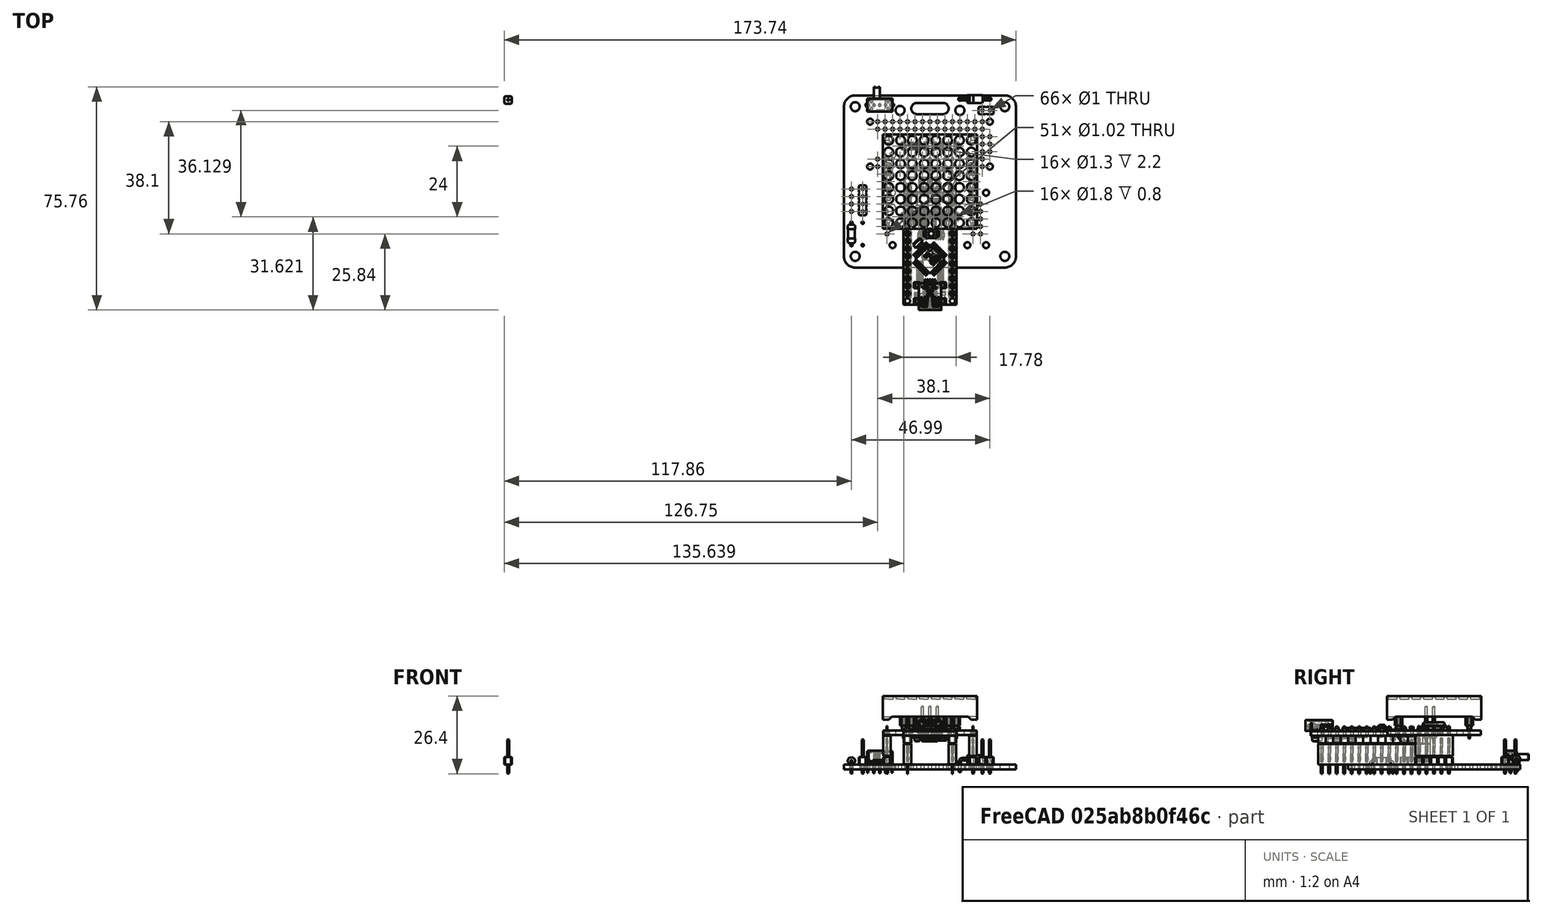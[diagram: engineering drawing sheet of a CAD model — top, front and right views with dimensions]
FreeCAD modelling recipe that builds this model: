
FCSTD DOCUMENT  (FreeCAD 0.20R29410 (Git))
Label: BagTag_v3
License: All rights reserved
LicenseURL: http://en.wikipedia.org/wiki/All_rights_reserved
objects: Part::Feature×202, App::Link×176, App::Part×9, Sketcher::SketchObject×3, PartDesign::CoordinateSystem×1
note: 206 computed .brp shape members not serialized (recipe doc carries the construction recipe); baked Part::Feature solids carry a one-line shape summary decoded from their .brp

FEATURE [PartDesign::CoordinateSystem] Local_CS_fc76
  AttacherType = Attacher::AttachEngine3D
  MapMode = 2
  Support = -> [X_Axis001]
FEATURE [Part::Feature] Pcb_fc76
  Placement = pos=(-88.9,83.82,0) rot=(0,0,1;0rad)
  shape: bbox 58.42 x 58.42 x 1.6 mm, 132 faces (baked)
FEATURE [Sketcher::SketchObject] PCB_Sketch_fc76
  FullyConstrained = false
  sketch-geometry (18):
    g0: LineSegment StartX=4.445 StartY=22.86 StartZ=0 EndX=-4.445 EndY=22.86 EndZ=0
    g1: LineSegment StartX=-25.4 StartY=29.21 StartZ=0 EndX=25.4 EndY=29.21 EndZ=0
    g2: LineSegment StartX=25.4 StartY=-29.21 StartZ=0 EndX=-25.4 EndY=-29.21 EndZ=0
    g3: LineSegment StartX=29.21 StartY=25.4 StartZ=0 EndX=29.21 EndY=-25.4 EndZ=0
    g4: LineSegment StartX=-4.445 StartY=26.67 StartZ=0 EndX=4.445 EndY=26.67 EndZ=0
    g5: LineSegment StartX=-29.21 StartY=-25.4 StartZ=0 EndX=-29.21 EndY=25.4 EndZ=0
    g6: ArcOfCircle CenterX=25.4 CenterY=25.4 CenterZ=0 NormalX=0 NormalY=0 NormalZ=-1 AngleXU=1.5708 Radius=3.81 StartAngle=0 EndAngle=1.5708
    g7: ArcOfCircle CenterX=-4.445 CenterY=24.765 CenterZ=0 NormalX=0 NormalY=0 NormalZ=-1 AngleXU=-1.5708 Radius=1.905 StartAngle=0 EndAngle=3.14159
    g8: ArcOfCircle CenterX=25.4 CenterY=-25.4 CenterZ=0 NormalX=0 NormalY=0 NormalZ=-1 AngleXU=3.14159 Radius=3.81 StartAngle=0 EndAngle=1.5708
    g9: ArcOfCircle CenterX=-25.4 CenterY=25.4 CenterZ=0 NormalX=0 NormalY=0 NormalZ=-1 AngleXU=-1.46676e-07 Radius=3.81 StartAngle=0 EndAngle=1.5708
    g10: ArcOfCircle CenterX=4.445 CenterY=24.765 CenterZ=0 NormalX=0 NormalY=0 NormalZ=-1 AngleXU=1.5708 Radius=1.905 StartAngle=0 EndAngle=3.14159
    g11: ArcOfCircle CenterX=-25.4 CenterY=-25.4 CenterZ=0 NormalX=0 NormalY=0 NormalZ=-1 AngleXU=-1.5708 Radius=3.81 StartAngle=0 EndAngle=1.5708
    g12: Circle CenterX=10.16 CenterY=24.13 CenterZ=0 NormalX=0 NormalY=0 NormalZ=1 AngleXU=0 Radius=1.54502
    g13: Circle CenterX=25.4 CenterY=25.4 CenterZ=0 NormalX=0 NormalY=0 NormalZ=1 AngleXU=0 Radius=1.524
    g14: Circle CenterX=-10.16 CenterY=24.13 CenterZ=0 NormalX=0 NormalY=0 NormalZ=1 AngleXU=0 Radius=1.524
    g15: Circle CenterX=-25.4 CenterY=-25.4 CenterZ=0 NormalX=0 NormalY=0 NormalZ=1 AngleXU=0 Radius=1.524
    g16: Circle CenterX=25.4 CenterY=-25.4 CenterZ=0 NormalX=0 NormalY=0 NormalZ=1 AngleXU=0 Radius=1.524
    g17: Circle CenterX=-25.4 CenterY=25.4 CenterZ=0 NormalX=0 NormalY=0 NormalZ=1 AngleXU=0 Radius=1.524
  constraints (12):
    c: Coincident(g5,g11)
    c: Coincident(g5,g9)
    c: Coincident(g2,g11)
    c: Coincident(g1,g9)
    c: Coincident(g0,g7)
    c: Coincident(g4,g7)
    c: Coincident(g0,g10)
    c: Coincident(g4,g10)
    c: Coincident(g2,g8)
    c: Coincident(g1,g6)
    c: Coincident(g3,g8)
    c: Coincident(g3,g6)
FEATURE [App::Part] Board_Geoms_fc76
  Group = -> [Pcb_fc76,PCB_Sketch_fc76]
  Origin = -> Origin
FEATURE [Part::Feature] Shape  label="J203_PinHeader_1x01_P254mm_Vertical_da6c4aed0287"
  Placement = pos=(-143.256,27.686,0) rot=(0,0,1;1.5708rad)
  shape: bbox 2.54 x 2.54 x 11.54 mm, 28 faces (baked)
FEATURE [App::Link] J203_PinHeader_1x01_P254mm_Vertical_da6c4aed0287_ln_  label="J129_PinHeader_1x01_P254mm_Vertical_773ae547e81d"
  LinkPlacement = pos=(-96.012,34.036,0) rot=(0,0,1;1.5708rad)
  LinkedObject = -> Shape
  Placement = pos=(-96.012,34.036,0) rot=(0,0,1;1.5708rad)
FEATURE [App::Link] J203_PinHeader_1x01_P254mm_Vertical_da6c4aed0287_ln_001  label="J118_PinHeader_1x01_P254mm_Vertical_5aa259a9185c"
  LinkPlacement = pos=(-98.552,39.116,0) rot=(0,0,1;1.5708rad)
  LinkedObject = -> Shape
  Placement = pos=(-98.552,39.116,0) rot=(0,0,1;1.5708rad)
FEATURE [App::Link] J203_PinHeader_1x01_P254mm_Vertical_da6c4aed0287_ln_002  label="J208_PinHeader_1x01_P254mm_Vertical_72f53bb47756"
  LinkPlacement = pos=(-143.256,25.146,0) rot=(0,0,1;1.5708rad)
  LinkedObject = -> Shape
  Placement = pos=(-143.256,25.146,0) rot=(0,0,1;1.5708rad)
FEATURE [App::Link] J203_PinHeader_1x01_P254mm_Vertical_da6c4aed0287_ln_003  label="J192_PinHeader_1x01_P254mm_Vertical_2792789bb18d"
  LinkPlacement = pos=(-130.556,22.098,0) rot=(0,0,1;1.5708rad)
  LinkedObject = -> Shape
  Placement = pos=(-130.556,22.098,0) rot=(0,0,1;1.5708rad)
FEATURE [App::Link] J203_PinHeader_1x01_P254mm_Vertical_da6c4aed0287_ln_004  label="J112_PinHeader_1x01_P254mm_Vertical_6a244c9ca252"
  LinkPlacement = pos=(-101.092,41.656,0) rot=(0,0,1;1.5708rad)
  LinkedObject = -> Shape
  Placement = pos=(-101.092,41.656,0) rot=(0,0,1;1.5708rad)
FEATURE [App::Link] J203_PinHeader_1x01_P254mm_Vertical_da6c4aed0287_ln_005  label="J137_PinHeader_1x01_P254mm_Vertical_9c543508d3f7"
  LinkPlacement = pos=(-101.092,28.956,0) rot=(0,0,1;1.5708rad)
  LinkedObject = -> Shape
  Placement = pos=(-101.092,28.956,0) rot=(0,0,1;1.5708rad)
FEATURE [App::Link] J203_PinHeader_1x01_P254mm_Vertical_da6c4aed0287_ln_006  label="J141_PinHeader_1x01_P254mm_Vertical_27754063a736"
  LinkPlacement = pos=(-103.632,26.416,0) rot=(0,0,1;1.5708rad)
  LinkedObject = -> Shape
  Placement = pos=(-103.632,26.416,0) rot=(0,0,1;1.5708rad)
FEATURE [App::Link] J203_PinHeader_1x01_P254mm_Vertical_da6c4aed0287_ln_007  label="J127_PinHeader_1x01_P254mm_Vertical_64cb25116942"
  LinkPlacement = pos=(-101.092,34.036,0) rot=(0,0,1;1.5708rad)
  LinkedObject = -> Shape
  Placement = pos=(-101.092,34.036,0) rot=(0,0,1;1.5708rad)
FEATURE [App::Link] J203_PinHeader_1x01_P254mm_Vertical_da6c4aed0287_ln_008  label="J109_PinHeader_1x01_P254mm_Vertical_46e97698a8e3"
  LinkPlacement = pos=(-96.012,44.196,0) rot=(0,0,1;1.5708rad)
  LinkedObject = -> Shape
  Placement = pos=(-96.012,44.196,0) rot=(0,0,1;1.5708rad)
FEATURE [App::Link] J203_PinHeader_1x01_P254mm_Vertical_da6c4aed0287_ln_009  label="J136_PinHeader_1x01_P254mm_Vertical_3277878d9fcc"
  LinkPlacement = pos=(-103.632,28.956,0) rot=(0,0,1;1.5708rad)
  LinkedObject = -> Shape
  Placement = pos=(-103.632,28.956,0) rot=(0,0,1;1.5708rad)
FEATURE [App::Link] J203_PinHeader_1x01_P254mm_Vertical_da6c4aed0287_ln_010  label="J174_PinHeader_1x01_P254mm_Vertical_6a619a310b17"
  LinkPlacement = pos=(-111.252,22.352,0) rot=(0,0,1;1.5708rad)
  LinkedObject = -> Shape
  Placement = pos=(-111.252,22.352,0) rot=(0,0,1;1.5708rad)
FEATURE [App::Link] J203_PinHeader_1x01_P254mm_Vertical_da6c4aed0287_ln_011  label="J163_PinHeader_1x01_P254mm_Vertical_eca1b71ce0e1"
  LinkPlacement = pos=(-113.792,27.432,0) rot=(0,0,1;1.5708rad)
  LinkedObject = -> Shape
  Placement = pos=(-113.792,27.432,0) rot=(0,0,1;1.5708rad)
FEATURE [App::Link] J203_PinHeader_1x01_P254mm_Vertical_da6c4aed0287_ln_012  label="J221_PinHeader_1x01_P254mm_Vertical_e87cc0828aff"
  LinkPlacement = pos=(-91.694,43.688,0) rot=(0,0,1;1.5708rad)
  LinkedObject = -> Shape
  Placement = pos=(-91.694,43.688,0) rot=(0,0,1;1.5708rad)
FEATURE [App::Link] J203_PinHeader_1x01_P254mm_Vertical_da6c4aed0287_ln_013  label="J145_PinHeader_1x01_P254mm_Vertical_00ab3d87ffcd"
  LinkPlacement = pos=(-106.172,23.876,0) rot=(0,0,1;1.5708rad)
  LinkedObject = -> Shape
  Placement = pos=(-106.172,23.876,0) rot=(0,0,1;1.5708rad)
FEATURE [App::Link] J203_PinHeader_1x01_P254mm_Vertical_da6c4aed0287_ln_014  label="J177_PinHeader_1x01_P254mm_Vertical_e80f5348a3fd"
  LinkPlacement = pos=(-116.332,19.812,0) rot=(0,0,1;1.5708rad)
  LinkedObject = -> Shape
  Placement = pos=(-116.332,19.812,0) rot=(0,0,1;1.5708rad)
FEATURE [App::Link] J203_PinHeader_1x01_P254mm_Vertical_da6c4aed0287_ln_015  label="J207_PinHeader_1x01_P254mm_Vertical_62e98df2bb86"
  LinkPlacement = pos=(-145.796,25.146,0) rot=(0,0,1;1.5708rad)
  LinkedObject = -> Shape
  Placement = pos=(-145.796,25.146,0) rot=(0,0,1;1.5708rad)
FEATURE [App::Link] J203_PinHeader_1x01_P254mm_Vertical_da6c4aed0287_ln_016  label="J191_PinHeader_1x01_P254mm_Vertical_de5b5ec60197"
  LinkPlacement = pos=(-133.096,22.098,0) rot=(0,0,1;1.5708rad)
  LinkedObject = -> Shape
  Placement = pos=(-133.096,22.098,0) rot=(0,0,1;1.5708rad)
FEATURE [App::Link] J203_PinHeader_1x01_P254mm_Vertical_da6c4aed0287_ln_017  label="J166_PinHeader_1x01_P254mm_Vertical_84919f920f7b"
  LinkPlacement = pos=(-118.872,24.892,0) rot=(0,0,1;1.5708rad)
  LinkedObject = -> Shape
  Placement = pos=(-118.872,24.892,0) rot=(0,0,1;1.5708rad)
FEATURE [App::Link] J203_PinHeader_1x01_P254mm_Vertical_da6c4aed0287_ln_018  label="J153_PinHeader_1x01_P254mm_Vertical_de25c8d6ebfc"
  LinkPlacement = pos=(-98.552,21.336,0) rot=(0,0,1;1.5708rad)
  LinkedObject = -> Shape
  Placement = pos=(-98.552,21.336,0) rot=(0,0,1;1.5708rad)
FEATURE [App::Link] J203_PinHeader_1x01_P254mm_Vertical_da6c4aed0287_ln_019  label="J146_PinHeader_1x01_P254mm_Vertical_6cd363f12a80"
  LinkPlacement = pos=(-103.632,23.876,0) rot=(0,0,1;1.5708rad)
  LinkedObject = -> Shape
  Placement = pos=(-103.632,23.876,0) rot=(0,0,1;1.5708rad)
FEATURE [App::Link] J203_PinHeader_1x01_P254mm_Vertical_da6c4aed0287_ln_020  label="J160_PinHeader_1x01_P254mm_Vertical_7b98299fb2b6"
  LinkPlacement = pos=(-121.412,27.432,0) rot=(0,0,1;1.5708rad)
  LinkedObject = -> Shape
  Placement = pos=(-121.412,27.432,0) rot=(0,0,1;1.5708rad)
FEATURE [App::Link] J203_PinHeader_1x01_P254mm_Vertical_da6c4aed0287_ln_021  label="J214_PinHeader_1x01_P254mm_Vertical_d33f2c13bd96"
  LinkPlacement = pos=(-140.716,22.606,0) rot=(0,0,1;1.5708rad)
  LinkedObject = -> Shape
  Placement = pos=(-140.716,22.606,0) rot=(0,0,1;1.5708rad)
FEATURE [App::Link] J203_PinHeader_1x01_P254mm_Vertical_da6c4aed0287_ln_022  label="J142_PinHeader_1x01_P254mm_Vertical_ebb3536fd29e"
  LinkPlacement = pos=(-101.092,26.416,0) rot=(0,0,1;1.5708rad)
  LinkedObject = -> Shape
  Placement = pos=(-101.092,26.416,0) rot=(0,0,1;1.5708rad)
FEATURE [App::Link] J203_PinHeader_1x01_P254mm_Vertical_da6c4aed0287_ln_023  label="J126_PinHeader_1x01_P254mm_Vertical_9a14729430aa"
  LinkPlacement = pos=(-103.632,34.036,0) rot=(0,0,1;1.5708rad)
  LinkedObject = -> Shape
  Placement = pos=(-103.632,34.036,0) rot=(0,0,1;1.5708rad)
FEATURE [App::Link] J203_PinHeader_1x01_P254mm_Vertical_da6c4aed0287_ln_024  label="J198_PinHeader_1x01_P254mm_Vertical_e60d4ac48af7"
  LinkPlacement = pos=(-128.016,19.558,0) rot=(0,0,1;1.5708rad)
  LinkedObject = -> Shape
  Placement = pos=(-128.016,19.558,0) rot=(0,0,1;1.5708rad)
FEATURE [App::Link] J203_PinHeader_1x01_P254mm_Vertical_da6c4aed0287_ln_025  label="J167_PinHeader_1x01_P254mm_Vertical_5f2264147a32"
  LinkPlacement = pos=(-116.332,24.892,0) rot=(0,0,1;1.5708rad)
  LinkedObject = -> Shape
  Placement = pos=(-116.332,24.892,0) rot=(0,0,1;1.5708rad)
FEATURE [App::Link] J203_PinHeader_1x01_P254mm_Vertical_da6c4aed0287_ln_026  label="J175_PinHeader_1x01_P254mm_Vertical_2f2c6f5fa7e0"
  LinkPlacement = pos=(-121.412,19.812,0) rot=(0,0,1;1.5708rad)
  LinkedObject = -> Shape
  Placement = pos=(-121.412,19.812,0) rot=(0,0,1;1.5708rad)
FEATURE [App::Link] J203_PinHeader_1x01_P254mm_Vertical_da6c4aed0287_ln_027  label="J185_PinHeader_1x01_P254mm_Vertical_64dd41409d9f"
  LinkPlacement = pos=(-135.636,24.638,0) rot=(0,0,1;1.5708rad)
  LinkedObject = -> Shape
  Placement = pos=(-135.636,24.638,0) rot=(0,0,1;1.5708rad)
FEATURE [App::Link] J203_PinHeader_1x01_P254mm_Vertical_da6c4aed0287_ln_028  label="J128_PinHeader_1x01_P254mm_Vertical_14a406c96dca"
  LinkPlacement = pos=(-98.552,34.036,0) rot=(0,0,1;1.5708rad)
  LinkedObject = -> Shape
  Placement = pos=(-98.552,34.036,0) rot=(0,0,1;1.5708rad)
FEATURE [App::Link] J203_PinHeader_1x01_P254mm_Vertical_da6c4aed0287_ln_029  label="J212_PinHeader_1x01_P254mm_Vertical_684e6d7036d3"
  LinkPlacement = pos=(-145.796,22.606,0) rot=(0,0,1;1.5708rad)
  LinkedObject = -> Shape
  Placement = pos=(-145.796,22.606,0) rot=(0,0,1;1.5708rad)
FEATURE [App::Link] J203_PinHeader_1x01_P254mm_Vertical_da6c4aed0287_ln_030  label="J181_PinHeader_1x01_P254mm_Vertical_3395830e7b0b"
  LinkPlacement = pos=(-133.096,27.178,0) rot=(0,0,1;1.5708rad)
  LinkedObject = -> Shape
  Placement = pos=(-133.096,27.178,0) rot=(0,0,1;1.5708rad)
FEATURE [App::Link] J203_PinHeader_1x01_P254mm_Vertical_da6c4aed0287_ln_031  label="J158_PinHeader_1x01_P254mm_Vertical_ad3d40650960"
  LinkPlacement = pos=(-98.552,18.796,0) rot=(0,0,1;1.5708rad)
  LinkedObject = -> Shape
  Placement = pos=(-98.552,18.796,0) rot=(0,0,1;1.5708rad)
FEATURE [App::Link] J203_PinHeader_1x01_P254mm_Vertical_da6c4aed0287_ln_032  label="J104_PinHeader_1x01_P254mm_Vertical_8b62ba1c48d5"
  LinkPlacement = pos=(-96.012,46.736,0) rot=(0,0,1;1.5708rad)
  LinkedObject = -> Shape
  Placement = pos=(-96.012,46.736,0) rot=(0,0,1;1.5708rad)
FEATURE [App::Link] J203_PinHeader_1x01_P254mm_Vertical_da6c4aed0287_ln_033  label="J197_PinHeader_1x01_P254mm_Vertical_d9d08025a7fb"
  LinkPlacement = pos=(-130.556,19.558,0) rot=(0,0,1;1.5708rad)
  LinkedObject = -> Shape
  Placement = pos=(-130.556,19.558,0) rot=(0,0,1;1.5708rad)
FEATURE [App::Link] J203_PinHeader_1x01_P254mm_Vertical_da6c4aed0287_ln_034  label="J195_PinHeader_1x01_P254mm_Vertical_3bb2cf8e585d"
  LinkPlacement = pos=(-135.636,19.558,0) rot=(0,0,1;1.5708rad)
  LinkedObject = -> Shape
  Placement = pos=(-135.636,19.558,0) rot=(0,0,1;1.5708rad)
FEATURE [App::Link] J203_PinHeader_1x01_P254mm_Vertical_da6c4aed0287_ln_035  label="J204_PinHeader_1x01_P254mm_Vertical_428c39a7f71f"
  LinkPlacement = pos=(-140.716,27.686,0) rot=(0,0,1;1.5708rad)
  LinkedObject = -> Shape
  Placement = pos=(-140.716,27.686,0) rot=(0,0,1;1.5708rad)
FEATURE [App::Link] J203_PinHeader_1x01_P254mm_Vertical_da6c4aed0287_ln_036  label="J242_PinHeader_1x01_P254mm_Vertical_00fbceee7ab9"
  LinkPlacement = pos=(-86.614,20.828,0) rot=(0,0,1;1.5708rad)
  LinkedObject = -> Shape
  Placement = pos=(-86.614,20.828,0) rot=(0,0,1;1.5708rad)
FEATURE [App::Link] J203_PinHeader_1x01_P254mm_Vertical_da6c4aed0287_ln_037  label="J235_PinHeader_1x01_P254mm_Vertical_68c39cdf1477"
  LinkPlacement = pos=(-86.614,38.608,0) rot=(0,0,1;1.5708rad)
  LinkedObject = -> Shape
  Placement = pos=(-86.614,38.608,0) rot=(0,0,1;1.5708rad)
FEATURE [App::Link] J203_PinHeader_1x01_P254mm_Vertical_da6c4aed0287_ln_038  label="J215_PinHeader_1x01_P254mm_Vertical_30fb8c6109c9"
  LinkPlacement = pos=(-150.876,20.066,0) rot=(0,0,1;1.5708rad)
  LinkedObject = -> Shape
  Placement = pos=(-150.876,20.066,0) rot=(0,0,1;1.5708rad)
FEATURE [App::Link] J203_PinHeader_1x01_P254mm_Vertical_da6c4aed0287_ln_039  label="J155_PinHeader_1x01_P254mm_Vertical_cbb93bdeda80"
  LinkPlacement = pos=(-106.172,18.796,0) rot=(0,0,1;1.5708rad)
  LinkedObject = -> Shape
  Placement = pos=(-106.172,18.796,0) rot=(0,0,1;1.5708rad)
FEATURE [App::Link] J203_PinHeader_1x01_P254mm_Vertical_da6c4aed0287_ln_040  label="J134_PinHeader_1x01_P254mm_Vertical_c71becf67217"
  LinkPlacement = pos=(-96.012,31.496,0) rot=(0,0,1;1.5708rad)
  LinkedObject = -> Shape
  Placement = pos=(-96.012,31.496,0) rot=(0,0,1;1.5708rad)
FEATURE [App::Link] J203_PinHeader_1x01_P254mm_Vertical_da6c4aed0287_ln_041  label="J216_PinHeader_1x01_P254mm_Vertical_3caf071db488"
  LinkPlacement = pos=(-148.336,20.066,0) rot=(0,0,1;1.5708rad)
  LinkedObject = -> Shape
  Placement = pos=(-148.336,20.066,0) rot=(0,0,1;1.5708rad)
FEATURE [App::Link] J203_PinHeader_1x01_P254mm_Vertical_da6c4aed0287_ln_042  label="J184_PinHeader_1x01_P254mm_Vertical_249d3775cc33"
  LinkPlacement = pos=(-125.476,27.178,0) rot=(0,0,1;1.5708rad)
  LinkedObject = -> Shape
  Placement = pos=(-125.476,27.178,0) rot=(0,0,1;1.5708rad)
FEATURE [App::Link] J203_PinHeader_1x01_P254mm_Vertical_da6c4aed0287_ln_043  label="J190_PinHeader_1x01_P254mm_Vertical_a719b4abe7b1"
  LinkPlacement = pos=(-135.636,22.098,0) rot=(0,0,1;1.5708rad)
  LinkedObject = -> Shape
  Placement = pos=(-135.636,22.098,0) rot=(0,0,1;1.5708rad)
FEATURE [Part::Feature] Part__Feature  label="FC_16_cp_sp"
  shape: bbox 31.75 x 31.75 x 1.6 mm, 36 faces (baked)
FEATURE [Part::Feature] Part__Feature001  label="FC_16_cp_sp001"
  shape: bbox 1.25 x 2 x 1.25 mm, 28 faces (baked)
FEATURE [Part::Feature] Part__Feature002  label="FC_16_cp_sp002"
  shape: bbox 32 x 32 x 13.3 mm, 258 faces (baked)
FEATURE [Part::Feature] Part__Feature003  label="FC_16_cp_sp003"
  shape: bbox 20.32 x 2.54 x 3 mm, 94 faces (baked)
FEATURE [Part::Feature] Part__Feature004  label="FC_16_cp_sp004"
  shape: bbox 1.8 x 1.8 x 7.4 mm, 10 faces (baked)
FEATURE [Part::Feature] Part__Feature005  label="FC_16_cp_sp005"
  shape: bbox 1.8 x 1.8 x 7.4 mm, 10 faces (baked)
FEATURE [Part::Feature] Part__Feature006  label="FC_16_cp_sp006"
  shape: bbox 1.8 x 1.8 x 7.4 mm, 10 faces (baked)
FEATURE [Part::Feature] Part__Feature007  label="FC_16_cp_sp007"
  shape: bbox 1.8 x 1.8 x 7.4 mm, 10 faces (baked)
FEATURE [Part::Feature] Part__Feature008  label="FC_16_cp_sp008"
  shape: bbox 1.8 x 1.8 x 7.4 mm, 10 faces (baked)
FEATURE [Part::Feature] Part__Feature009  label="FC_16_cp_sp009"
  shape: bbox 1.8 x 1.8 x 7.4 mm, 10 faces (baked)
FEATURE [Part::Feature] Part__Feature010  label="FC_16_cp_sp010"
  shape: bbox 1.8 x 1.8 x 7.4 mm, 10 faces (baked)
FEATURE [Part::Feature] Part__Feature011  label="FC_16_cp_sp011"
  shape: bbox 1.8 x 1.8 x 7.4 mm, 10 faces (baked)
FEATURE [Part::Feature] Part__Feature012  label="FC_16_cp_sp012"
  shape: bbox 1 x 1 x 2.04 mm, 27 faces (baked)
FEATURE [Part::Feature] Part__Feature013  label="FC_16_cp_sp013"
  shape: bbox 1 x 1 x 2.04 mm, 27 faces (baked)
FEATURE [Part::Feature] Part__Feature014  label="FC_16_cp_sp014"
  shape: bbox 1 x 1 x 2.04 mm, 27 faces (baked)
FEATURE [Part::Feature] Part__Feature015  label="FC_16_cp_sp015"
  shape: bbox 1 x 1 x 2.04 mm, 27 faces (baked)
FEATURE [Part::Feature] Part__Feature016  label="FC_16_cp_sp016"
  shape: bbox 1 x 1 x 2.04 mm, 27 faces (baked)
FEATURE [Part::Feature] Part__Feature017  label="FC_16_cp_sp017"
  shape: bbox 1 x 1 x 2.04 mm, 27 faces (baked)
FEATURE [Part::Feature] Part__Feature018  label="FC_16_cp_sp018"
  shape: bbox 1 x 1 x 2.04 mm, 27 faces (baked)
FEATURE [Part::Feature] Part__Feature019  label="FC_16_cp_sp019"
  shape: bbox 1 x 1 x 2.04 mm, 27 faces (baked)
FEATURE [Part::Feature] Part__Feature020  label="FC_16_cp_sp020"
  shape: bbox 20.32 x 2.54 x 3 mm, 94 faces (baked)
FEATURE [Part::Feature] Part__Feature021  label="FC_16_cp_sp021"
  shape: bbox 1.8 x 1.8 x 7.4 mm, 10 faces (baked)
FEATURE [Part::Feature] Part__Feature022  label="FC_16_cp_sp022"
  shape: bbox 1.8 x 1.8 x 7.4 mm, 10 faces (baked)
FEATURE [Part::Feature] Part__Feature023  label="FC_16_cp_sp023"
  shape: bbox 1.8 x 1.8 x 7.4 mm, 10 faces (baked)
FEATURE [Part::Feature] Part__Feature024  label="FC_16_cp_sp024"
  shape: bbox 1.8 x 1.8 x 7.4 mm, 10 faces (baked)
FEATURE [Part::Feature] Part__Feature025  label="FC_16_cp_sp025"
  shape: bbox 1.8 x 1.8 x 7.4 mm, 10 faces (baked)
FEATURE [Part::Feature] Part__Feature026  label="FC_16_cp_sp026"
  shape: bbox 1.8 x 1.8 x 7.4 mm, 10 faces (baked)
FEATURE [Part::Feature] Part__Feature027  label="FC_16_cp_sp027"
  shape: bbox 1.8 x 1.8 x 7.4 mm, 10 faces (baked)
FEATURE [Part::Feature] Part__Feature028  label="FC_16_cp_sp028"
  shape: bbox 1.8 x 1.8 x 7.4 mm, 10 faces (baked)
FEATURE [Part::Feature] Part__Feature029  label="FC_16_cp_sp029"
  shape: bbox 1 x 1 x 2.04 mm, 27 faces (baked)
FEATURE [Part::Feature] Part__Feature030  label="FC_16_cp_sp030"
  shape: bbox 1 x 1 x 2.04 mm, 27 faces (baked)
FEATURE [Part::Feature] Part__Feature031  label="FC_16_cp_sp031"
  shape: bbox 1 x 1 x 2.04 mm, 27 faces (baked)
FEATURE [Part::Feature] Part__Feature032  label="FC_16_cp_sp032"
  shape: bbox 1 x 1 x 2.04 mm, 27 faces (baked)
FEATURE [Part::Feature] Part__Feature033  label="FC_16_cp_sp033"
  shape: bbox 1 x 1 x 2.04 mm, 27 faces (baked)
FEATURE [Part::Feature] Part__Feature034  label="FC_16_cp_sp034"
  shape: bbox 1 x 1 x 2.04 mm, 27 faces (baked)
FEATURE [Part::Feature] Part__Feature035  label="FC_16_cp_sp035"
  shape: bbox 1 x 1 x 2.04 mm, 27 faces (baked)
FEATURE [Part::Feature] Part__Feature036  label="FC_16_cp_sp036"
  shape: bbox 1 x 1 x 2.04 mm, 27 faces (baked)
FEATURE [Part::Feature] Part__Feature037  label="FC_16_cp_sp037"
  shape: bbox 2 x 1.2 x 0.45 mm, 26 faces (baked)
FEATURE [Part::Feature] Part__Feature038  label="FC_16_cp_sp038"
  shape: bbox 15.4 x 10.3 x 2.75 mm, 396 faces (baked)
FEATURE [Part::Feature] Part__Feature039  label="FC_16_cp_sp039"
  shape: bbox 2 x 1.25 x 1.25 mm, 28 faces (baked)
FEATURE [Part::Feature] Part__Feature040  label="FC_16_cp_sp040"
  shape: bbox 2.54 x 12.7 x 10.1 mm, 165 faces (baked)
FEATURE [Part::Feature] Part__Feature041  label="FC_16_cp_sp041"
  shape: bbox 2.54 x 12.7 x 10.1 mm, 165 faces (baked)
FEATURE [Part::Feature] Part__Feature042  label="FC_16_cp_sp042"
  shape: bbox 2.54 x 12.7 x 11.54 mm, 124 faces (baked)
FEATURE [Part::Feature] Part__Feature043  label="FC_16_cp_sp043"
  shape: bbox 2.54 x 12.7 x 11.54 mm, 124 faces (baked)
FEATURE [Part::Feature] Part__Feature044  label="FC_16_cp_sp044"
  shape: bbox 31.6 x 31.6 x 2e-07 mm, 1 faces, 0 solids (baked)
FEATURE [Part::Feature] Part__Feature045  label="FC_16_cp_sp045"
  shape: bbox 0.385 x 9.655 x 2e-07 mm, 1 faces, 0 solids (baked)
FEATURE [Part::Feature] Part__Feature046  label="FC_16_cp_sp046"
  shape: bbox 0.385 x 7.84 x 2e-07 mm, 1 faces, 0 solids (baked)
FEATURE [Part::Feature] Part__Feature047  label="FC_16_cp_sp047"
  shape: bbox 5.284 x 2.531 x 2e-07 mm, 1 faces, 0 solids (baked)
FEATURE [Part::Feature] Part__Feature048  label="FC_16_cp_sp048"
  shape: bbox 3.957 x 2.466 x 2e-07 mm, 1 faces, 0 solids (baked)
FEATURE [Part::Feature] Part__Feature049  label="FC_16_cp_sp049"
  shape: bbox 3.273 x 1.422 x 2e-07 mm, 1 faces, 0 solids (baked)
FEATURE [Part::Feature] Part__Feature050  label="FC_16_cp_sp050"
  shape: bbox 3.273 x 1.422 x 2e-07 mm, 1 faces, 0 solids (baked)
FEATURE [Part::Feature] Part__Feature051  label="FC_16_cp_sp051"
  shape: bbox 3.273 x 1.422 x 2e-07 mm, 1 faces, 0 solids (baked)
FEATURE [Part::Feature] Part__Feature052  label="FC_16_cp_sp052"
  shape: bbox 3.273 x 1.422 x 2e-07 mm, 1 faces, 0 solids (baked)
FEATURE [Part::Feature] Part__Feature053  label="FC_16_cp_sp053"
  shape: bbox 3.273 x 1.422 x 2e-07 mm, 1 faces, 0 solids (baked)
FEATURE [Part::Feature] Part__Feature054  label="FC_16_cp_sp054"
  shape: bbox 3.273 x 1.422 x 2e-07 mm, 1 faces, 0 solids (baked)
FEATURE [Part::Feature] Part__Feature055  label="FC_16_cp_sp055"
  shape: bbox 3.273 x 1.422 x 2e-07 mm, 1 faces, 0 solids (baked)
FEATURE [Part::Feature] Part__Feature056  label="FC_16_cp_sp056"
  shape: bbox 3.273 x 1.422 x 2e-07 mm, 1 faces, 0 solids (baked)
FEATURE [Part::Feature] Part__Feature057  label="FC_16_cp_sp057"
  shape: bbox 3.273 x 1.422 x 2e-07 mm, 1 faces, 0 solids (baked)
FEATURE [Part::Feature] Part__Feature058  label="FC_16_cp_sp058"
  shape: bbox 3.267 x 1.403 x 2e-07 mm, 1 faces, 0 solids (baked)
FEATURE [Part::Feature] Part__Feature059  label="FC_16_cp_sp059"
  shape: bbox 1.15 x 0.7688 x 2e-07 mm, 1 faces, 0 solids (baked)
FEATURE [Part::Feature] Part__Feature060  label="FC_16_cp_sp060"
  shape: bbox 1.15 x 0.7687 x 2e-07 mm, 1 faces, 0 solids (baked)
FEATURE [Part::Feature] Part__Feature061  label="FC_16_cp_sp061"
  shape: bbox 1.15 x 0.7687 x 2e-07 mm, 1 faces, 0 solids (baked)
FEATURE [Part::Feature] Part__Feature062  label="FC_16_cp_sp062"
  shape: bbox 1.15 x 0.7687 x 2e-07 mm, 1 faces, 0 solids (baked)
FEATURE [Part::Feature] Part__Feature063  label="FC_16_cp_sp063"
  shape: bbox 1.149 x 0.7214 x 2e-07 mm, 1 faces, 0 solids (baked)
FEATURE [Part::Feature] Part__Feature064  label="FC_16_cp_sp064"
  shape: bbox 1.149 x 0.7214 x 2e-07 mm, 1 faces, 0 solids (baked)
FEATURE [Part::Feature] Part__Feature065  label="FC_16_cp_sp065"
  shape: bbox 1.15 x 0.7192 x 2e-07 mm, 1 faces, 0 solids (baked)
FEATURE [Part::Feature] Part__Feature066  label="FC_16_cp_sp066"
  shape: bbox 1.15 x 0.7192 x 2e-07 mm, 1 faces, 0 solids (baked)
FEATURE [Part::Feature] Part__Feature067  label="FC_16_cp_sp067"
  shape: bbox 1.15 x 0.7192 x 2e-07 mm, 1 faces, 0 solids (baked)
FEATURE [Part::Feature] Part__Feature068  label="FC_16_cp_sp068"
  shape: bbox 1.15 x 0.7191 x 2e-07 mm, 1 faces, 0 solids (baked)
FEATURE [Part::Feature] Part__Feature069  label="FC_16_cp_sp069"
  shape: bbox 1.145 x 0.719 x 2e-07 mm, 1 faces, 0 solids (baked)
FEATURE [Part::Feature] Part__Feature070  label="FC_16_cp_sp070"
  shape: bbox 1.145 x 0.719 x 2e-07 mm, 1 faces, 0 solids (baked)
FEATURE [Part::Feature] Part__Feature071  label="FC_16_cp_sp071"
  shape: bbox 1.096 x 0.7666 x 2e-07 mm, 1 faces, 0 solids (baked)
FEATURE [Part::Feature] Part__Feature072  label="FC_16_cp_sp072"
  shape: bbox 1.1 x 0.719 x 2e-07 mm, 1 faces, 0 solids (baked)
FEATURE [Part::Feature] Part__Feature073  label="FC_16_cp_sp073"
  shape: bbox 1.1 x 0.719 x 2e-07 mm, 1 faces, 0 solids (baked)
FEATURE [Part::Feature] Part__Feature074  label="FC_16_cp_sp074"
  shape: bbox 1.1 x 0.719 x 2e-07 mm, 1 faces, 0 solids (baked)
FEATURE [Part::Feature] Part__Feature075  label="FC_16_cp_sp075"
  shape: bbox 1.1 x 0.719 x 2e-07 mm, 1 faces, 0 solids (baked)
FEATURE [Part::Feature] Part__Feature076  label="FC_16_cp_sp076"
  shape: bbox 1.1 x 0.719 x 2e-07 mm, 1 faces, 0 solids (baked)
FEATURE [Part::Feature] Part__Feature077  label="FC_16_cp_sp077"
  shape: bbox 1.1 x 0.719 x 2e-07 mm, 1 faces, 0 solids (baked)
FEATURE [Part::Feature] Part__Feature078  label="FC_16_cp_sp078"
  shape: bbox 1.1 x 0.719 x 2e-07 mm, 1 faces, 0 solids (baked)
FEATURE [Part::Feature] Part__Feature079  label="FC_16_cp_sp079"
  shape: bbox 1.1 x 0.719 x 2e-07 mm, 1 faces, 0 solids (baked)
FEATURE [Part::Feature] Part__Feature080  label="FC_16_cp_sp080"
  shape: bbox 1.1 x 0.719 x 2e-07 mm, 1 faces, 0 solids (baked)
FEATURE [Part::Feature] Part__Feature081  label="FC_16_cp_sp081"
  shape: bbox 1.1 x 0.719 x 2e-07 mm, 1 faces, 0 solids (baked)
FEATURE [Part::Feature] Part__Feature082  label="FC_16_cp_sp082"
  shape: bbox 1.1 x 0.719 x 2e-07 mm, 1 faces, 0 solids (baked)
FEATURE [Part::Feature] Part__Feature083  label="FC_16_cp_sp083"
  shape: bbox 1.1 x 0.719 x 2e-07 mm, 1 faces, 0 solids (baked)
FEATURE [Part::Feature] Part__Feature084  label="FC_16_cp_sp084"
  shape: bbox 1.1 x 0.719 x 2e-07 mm, 1 faces, 0 solids (baked)
FEATURE [Part::Feature] Part__Feature085  label="FC_16_cp_sp085"
  shape: bbox 1.1 x 0.6715 x 2e-07 mm, 1 faces, 0 solids (baked)
FEATURE [Part::Feature] Part__Feature086  label="FC_16_cp_sp086"
  shape: bbox 1.1 x 0.6715 x 2e-07 mm, 1 faces, 0 solids (baked)
FEATURE [Part::Feature] Part__Feature087  label="FC_16_cp_sp087"
  shape: bbox 1.1 x 0.6714 x 2e-07 mm, 1 faces, 0 solids (baked)
FEATURE [Part::Feature] Part__Feature088  label="FC_16_cp_sp088"
  shape: bbox 1.1 x 0.6714 x 2e-07 mm, 1 faces, 0 solids (baked)
FEATURE [Part::Feature] Part__Feature089  label="FC_16_cp_sp089"
  shape: bbox 1.1 x 0.6714 x 2e-07 mm, 1 faces, 0 solids (baked)
FEATURE [Part::Feature] Part__Feature090  label="FC_16_cp_sp090"
  shape: bbox 1.1 x 0.6714 x 2e-07 mm, 1 faces, 0 solids (baked)
FEATURE [Part::Feature] Part__Feature091  label="FC_16_cp_sp091"
  shape: bbox 1.1 x 0.6714 x 2e-07 mm, 1 faces, 0 solids (baked)
FEATURE [Part::Feature] Part__Feature092  label="FC_16_cp_sp092"
  shape: bbox 1.1 x 0.6714 x 2e-07 mm, 1 faces, 0 solids (baked)
FEATURE [Part::Feature] Part__Feature093  label="FC_16_cp_sp093"
  shape: bbox 1.1 x 0.6714 x 2e-07 mm, 1 faces, 0 solids (baked)
FEATURE [Part::Feature] Part__Feature094  label="FC_16_cp_sp094"
  shape: bbox 1.1 x 0.6714 x 2e-07 mm, 1 faces, 0 solids (baked)
FEATURE [Part::Feature] Part__Feature095  label="FC_16_cp_sp095"
  shape: bbox 1.1 x 0.6714 x 2e-07 mm, 1 faces, 0 solids (baked)
FEATURE [Part::Feature] Part__Feature096  label="FC_16_cp_sp096"
  shape: bbox 1.1 x 0.6714 x 2e-07 mm, 1 faces, 0 solids (baked)
FEATURE [Part::Feature] Part__Feature097  label="FC_16_cp_sp097"
  shape: bbox 1.1 x 0.6714 x 2e-07 mm, 1 faces, 0 solids (baked)
FEATURE [Part::Feature] Part__Feature098  label="FC_16_cp_sp098"
  shape: bbox 1.1 x 0.6714 x 2e-07 mm, 1 faces, 0 solids (baked)
FEATURE [Part::Feature] Part__Feature099  label="FC_16_cp_sp099"
  shape: bbox 1.1 x 0.6714 x 2e-07 mm, 1 faces, 0 solids (baked)
FEATURE [Part::Feature] Part__Feature100  label="FC_16_cp_sp100"
  shape: bbox 1.1 x 0.6714 x 2e-07 mm, 1 faces, 0 solids (baked)
FEATURE [Part::Feature] Part__Feature101  label="FC_16_cp_sp101"
  shape: bbox 1.1 x 0.6714 x 2e-07 mm, 1 faces, 0 solids (baked)
FEATURE [Part::Feature] Part__Feature102  label="FC_16_cp_sp102"
  shape: bbox 1.1 x 0.6714 x 2e-07 mm, 1 faces, 0 solids (baked)
FEATURE [Part::Feature] Part__Feature103  label="FC_16_cp_sp103"
  shape: bbox 1.1 x 0.6714 x 2e-07 mm, 1 faces, 0 solids (baked)
FEATURE [Part::Feature] Part__Feature104  label="FC_16_cp_sp104"
  shape: bbox 1.149 x 0.5298 x 2e-07 mm, 1 faces, 0 solids (baked)
FEATURE [Part::Feature] Part__Feature105  label="FC_16_cp_sp105"
  shape: bbox 1.149 x 0.5298 x 2e-07 mm, 1 faces, 0 solids (baked)
FEATURE [Part::Feature] Part__Feature106  label="FC_16_cp_sp106"
  shape: bbox 1.1 x 0.5762 x 2e-07 mm, 1 faces, 0 solids (baked)
FEATURE [Part::Feature] Part__Feature107  label="FC_16_cp_sp107"
  shape: bbox 1.1 x 0.5762 x 2e-07 mm, 1 faces, 0 solids (baked)
FEATURE [Part::Feature] Part__Feature108  label="FC_16_cp_sp108"
  shape: bbox 0.4667 x 1.029 x 2e-07 mm, 1 faces, 0 solids (baked)
FEATURE [Part::Feature] Part__Feature109  label="FC_16_cp_sp109"
  shape: bbox 0.3111 x 0.6858 x 2e-07 mm, 1 faces, 0 solids (baked)
FEATURE [Part::Feature] Part__Feature110  label="FC_16_cp_sp110"
  shape: bbox 0.2715 x 0.6668 x 2e-07 mm, 1 faces, 0 solids (baked)
FEATURE [Part::Feature] Part__Feature111  label="FC_16_cp_sp111"
  shape: bbox 0.2714 x 0.6668 x 2e-07 mm, 1 faces, 0 solids (baked)
FEATURE [Part::Feature] Part__Feature112  label="FC_16_cp_sp112"
  shape: bbox 0.2714 x 0.6668 x 2e-07 mm, 1 faces, 0 solids (baked)
FEATURE [Part::Feature] Part__Feature113  label="FC_16_cp_sp113"
  shape: bbox 0.2714 x 0.6668 x 2e-07 mm, 1 faces, 0 solids (baked)
FEATURE [Part::Feature] Part__Feature114  label="FC_16_cp_sp114"
  shape: bbox 0.6426 x 0.12 x 2e-07 mm, 1 faces, 0 solids (baked)
FEATURE [Part::Feature] Part__Feature115  label="FC_16_cp_sp115"
  shape: bbox 0.12 x 0.6426 x 2e-07 mm, 1 faces, 0 solids (baked)
FEATURE [Part::Feature] Part__Feature116  label="FC_16_cp_sp116"
  shape: bbox 0.12 x 0.6426 x 2e-07 mm, 1 faces, 0 solids (baked)
FEATURE [Part::Feature] Part__Feature117  label="FC_16_cp_sp117"
  shape: bbox 0.6426 x 0.12 x 2e-07 mm, 1 faces, 0 solids (baked)
FEATURE [Part::Feature] Part__Feature118  label="FC_16_cp_sp118"
  shape: bbox 0.5742 x 0.12 x 2e-07 mm, 1 faces, 0 solids (baked)
FEATURE [Part::Feature] Part__Feature119  label="FC_16_cp_sp119"
  shape: bbox 0.5742 x 0.12 x 2e-07 mm, 1 faces, 0 solids (baked)
FEATURE [App::Part] FC_16_cp_sp  label="LED2_FC_16_cp_sp120_3c06c14edb76"
  Group = -> [Part__Feature,Part__Feature001,Part__Feature002,Part__Feature003,Part__Feature004,Part__Feature005,Part__Feature006,Part__Feature007,Part__Feature008,Part__Feature009,Part__Feature010,Part__Feature011,Part__Feature012,Part__Feature013,Part__Feature014,Part__Feature015,Part__Feature016,Part__Feature017,Part__Feature018,Part__Feature019,Part__Feature020,Part__Feature021,Part__Feature022,+97 more]
  Origin = -> Origin008
  Placement = pos=(31.75,-12.7,0) rot=(0,0,1;0rad)
FEATURE [App::Link] J203_PinHeader_1x01_P254mm_Vertical_da6c4aed0287_ln_044  label="J187_PinHeader_1x01_P254mm_Vertical_f1aa55f767d0"
  LinkPlacement = pos=(-130.556,24.638,0) rot=(0,0,1;1.5708rad)
  LinkedObject = -> Shape
  Placement = pos=(-130.556,24.638,0) rot=(0,0,1;1.5708rad)
FEATURE [App::Link] J203_PinHeader_1x01_P254mm_Vertical_da6c4aed0287_ln_045  label="J201_PinHeader_1x01_P254mm_Vertical_cecdf641149b"
  LinkPlacement = pos=(-148.336,27.686,0) rot=(0,0,1;1.5708rad)
  LinkedObject = -> Shape
  Placement = pos=(-148.336,27.686,0) rot=(0,0,1;1.5708rad)
FEATURE [App::Link] J203_PinHeader_1x01_P254mm_Vertical_da6c4aed0287_ln_046  label="J234_PinHeader_1x01_P254mm_Vertical_5beb73ee3343"
  LinkPlacement = pos=(-86.614,41.148,0) rot=(0,0,1;1.5708rad)
  LinkedObject = -> Shape
  Placement = pos=(-86.614,41.148,0) rot=(0,0,1;1.5708rad)
FEATURE [App::Link] J203_PinHeader_1x01_P254mm_Vertical_da6c4aed0287_ln_047  label="J210_PinHeader_1x01_P254mm_Vertical_d780b6723fc1"
  LinkPlacement = pos=(-150.876,22.606,0) rot=(0,0,1;1.5708rad)
  LinkedObject = -> Shape
  Placement = pos=(-150.876,22.606,0) rot=(0,0,1;1.5708rad)
FEATURE [App::Link] J203_PinHeader_1x01_P254mm_Vertical_da6c4aed0287_ln_048  label="J186_PinHeader_1x01_P254mm_Vertical_971ca6a70be6"
  LinkPlacement = pos=(-133.096,24.638,0) rot=(0,0,1;1.5708rad)
  LinkedObject = -> Shape
  Placement = pos=(-133.096,24.638,0) rot=(0,0,1;1.5708rad)
FEATURE [App::Link] J203_PinHeader_1x01_P254mm_Vertical_da6c4aed0287_ln_049  label="J113_PinHeader_1x01_P254mm_Vertical_037e9dbc6d28"
  LinkPlacement = pos=(-98.552,41.656,0) rot=(0,0,1;1.5708rad)
  LinkedObject = -> Shape
  Placement = pos=(-98.552,41.656,0) rot=(0,0,1;1.5708rad)
FEATURE [App::Link] J203_PinHeader_1x01_P254mm_Vertical_da6c4aed0287_ln_050  label="J156_PinHeader_1x01_P254mm_Vertical_f91dea8db7ee"
  LinkPlacement = pos=(-103.632,18.796,0) rot=(0,0,1;1.5708rad)
  LinkedObject = -> Shape
  Placement = pos=(-103.632,18.796,0) rot=(0,0,1;1.5708rad)
FEATURE [App::Link] J203_PinHeader_1x01_P254mm_Vertical_da6c4aed0287_ln_051  label="J193_PinHeader_1x01_P254mm_Vertical_db89102eea80"
  LinkPlacement = pos=(-128.016,22.098,0) rot=(0,0,1;1.5708rad)
  LinkedObject = -> Shape
  Placement = pos=(-128.016,22.098,0) rot=(0,0,1;1.5708rad)
FEATURE [App::Link] J203_PinHeader_1x01_P254mm_Vertical_da6c4aed0287_ln_052  label="J125_PinHeader_1x01_P254mm_Vertical_bb6de2ac7262"
  LinkPlacement = pos=(-106.172,34.036,0) rot=(0,0,1;1.5708rad)
  LinkedObject = -> Shape
  Placement = pos=(-106.172,34.036,0) rot=(0,0,1;1.5708rad)
FEATURE [App::Link] J203_PinHeader_1x01_P254mm_Vertical_da6c4aed0287_ln_053  label="J232_PinHeader_1x01_P254mm_Vertical_094d27a21353"
  LinkPlacement = pos=(-86.614,46.228,0) rot=(0,0,1;1.5708rad)
  LinkedObject = -> Shape
  Placement = pos=(-86.614,46.228,0) rot=(0,0,1;1.5708rad)
FEATURE [App::Link] J203_PinHeader_1x01_P254mm_Vertical_da6c4aed0287_ln_054  label="J238_PinHeader_1x01_P254mm_Vertical_29d09037a46b"
  LinkPlacement = pos=(-86.614,30.988,0) rot=(0,0,1;1.5708rad)
  LinkedObject = -> Shape
  Placement = pos=(-86.614,30.988,0) rot=(0,0,1;1.5708rad)
FEATURE [Part::Feature] Shape001  label="BT1_PinHeader_1x02_P254mm_Vertical_64228b7c207f"
  Placement = pos=(20.32,24.13,0) rot=(0,0,-1;1.5708rad)
  shape: bbox 5.08 x 2.54 x 11.54 mm, 52 faces (baked)
FEATURE [Part::Feature] Part__Feature120  label="pp3_battery"
  shape: bbox 1.5 x 6.35 x 6.35 mm, 3 faces, 0 solids (baked)
FEATURE [Part::Feature] Part__Feature121  label="pp3_battery001"
  shape: bbox 42.82 x 26 x 16.6 mm, 196 faces, 0 solids (baked)
FEATURE [Part::Feature] Part__Feature122  label="pp3_battery002"
  shape: bbox 3.2 x 8 x 8 mm, 11 faces, 0 solids (baked)
FEATURE [Part::Feature] Part__Feature123  label="pp3_battery003"
  shape: bbox 0.0001965 x 6.345 x 2.963e-07 mm, 1 faces, 0 solids (baked)
FEATURE [Part::Feature] Part__Feature124  label="pp3_battery004"
  shape: bbox 0.8457 x 25.33 x 15.74 mm, 1 faces, 0 solids (baked)
FEATURE [Part::Feature] Part__Feature125  label="pp3_battery005"
  shape: bbox 0.0001967 x 6.334 x 2.965e-07 mm, 1 faces, 0 solids (baked)
FEATURE [Part::Feature] Part__Feature126  label="pp3_battery006"
  shape: bbox 0.0001965 x 6.345 x 2.963e-07 mm, 1 faces, 0 solids (baked)
FEATURE [Part::Feature] Part__Feature127  label="pp3_battery007"
  shape: bbox 0.0001967 x 6.334 x 2.965e-07 mm, 1 faces, 0 solids (baked)
FEATURE [Part::Feature] Part__Feature128  label="pp3_battery008"
  shape: bbox 3 x 8.776 x 7.6 mm, 28 faces, 0 solids (baked)
FEATURE [App::Part] pp3_battery  label="BT1_pp3_battery009_64228b7c207f[2]"
  Group = -> [Part__Feature120,Part__Feature121,Part__Feature122,Part__Feature123,Part__Feature124,Part__Feature125,Part__Feature126,Part__Feature127,Part__Feature128]
  Origin = -> Origin009
  Placement = pos=(19.05,48.26,-1.27) rot=(0,0,-1;1.5708rad)
FEATURE [App::Link] J203_PinHeader_1x01_P254mm_Vertical_da6c4aed0287_ln_055  label="J117_PinHeader_1x01_P254mm_Vertical_22706fc6efa7"
  LinkPlacement = pos=(-101.092,39.116,0) rot=(0,0,1;1.5708rad)
  LinkedObject = -> Shape
  Placement = pos=(-101.092,39.116,0) rot=(0,0,1;1.5708rad)
FEATURE [App::Link] J203_PinHeader_1x01_P254mm_Vertical_da6c4aed0287_ln_056  label="J119_PinHeader_1x01_P254mm_Vertical_2f136b6726bd"
  LinkPlacement = pos=(-96.012,39.116,0) rot=(0,0,1;1.5708rad)
  LinkedObject = -> Shape
  Placement = pos=(-96.012,39.116,0) rot=(0,0,1;1.5708rad)
FEATURE [App::Link] J203_PinHeader_1x01_P254mm_Vertical_da6c4aed0287_ln_057  label="J154_PinHeader_1x01_P254mm_Vertical_1ae400d14a7d"
  LinkPlacement = pos=(-96.012,21.336,0) rot=(0,0,1;1.5708rad)
  LinkedObject = -> Shape
  Placement = pos=(-96.012,21.336,0) rot=(0,0,1;1.5708rad)
FEATURE [App::Link] J203_PinHeader_1x01_P254mm_Vertical_da6c4aed0287_ln_058  label="J161_PinHeader_1x01_P254mm_Vertical_004e2b5e8ed7"
  LinkPlacement = pos=(-118.872,27.432,0) rot=(0,0,1;1.5708rad)
  LinkedObject = -> Shape
  Placement = pos=(-118.872,27.432,0) rot=(0,0,1;1.5708rad)
FEATURE [App::Link] J203_PinHeader_1x01_P254mm_Vertical_da6c4aed0287_ln_059  label="J120_PinHeader_1x01_P254mm_Vertical_5215226168a0"
  LinkPlacement = pos=(-106.172,36.576,0) rot=(0,0,1;1.5708rad)
  LinkedObject = -> Shape
  Placement = pos=(-106.172,36.576,0) rot=(0,0,1;1.5708rad)
FEATURE [App::Link] J203_PinHeader_1x01_P254mm_Vertical_da6c4aed0287_ln_060  label="J139_PinHeader_1x01_P254mm_Vertical_6fa549b88633"
  LinkPlacement = pos=(-96.012,28.956,0) rot=(0,0,1;1.5708rad)
  LinkedObject = -> Shape
  Placement = pos=(-96.012,28.956,0) rot=(0,0,1;1.5708rad)
FEATURE [App::Link] J203_PinHeader_1x01_P254mm_Vertical_da6c4aed0287_ln_061  label="J239_PinHeader_1x01_P254mm_Vertical_916bd54bab8a"
  LinkPlacement = pos=(-86.614,28.448,0) rot=(0,0,1;1.5708rad)
  LinkedObject = -> Shape
  Placement = pos=(-86.614,28.448,0) rot=(0,0,1;1.5708rad)
FEATURE [Part::Feature] Shape002  label="J2_PinHeader_1x04_P254mm_Vertical_b8c18ff84878"
  Placement = pos=(-22.86,-10.16,0) rot=(0,0,1;3.14159rad)
  shape: bbox 2.54 x 10.16 x 11.54 mm, 100 faces (baked)
FEATURE [App::Link] J203_PinHeader_1x01_P254mm_Vertical_da6c4aed0287_ln_062  label="J168_PinHeader_1x01_P254mm_Vertical_9d3dc9451df2"
  LinkPlacement = pos=(-113.792,24.892,0) rot=(0,0,1;1.5708rad)
  LinkedObject = -> Shape
  Placement = pos=(-113.792,24.892,0) rot=(0,0,1;1.5708rad)
FEATURE [App::Link] J203_PinHeader_1x01_P254mm_Vertical_da6c4aed0287_ln_063  label="J148_PinHeader_1x01_P254mm_Vertical_6b9a9c7a9553"
  LinkPlacement = pos=(-98.552,23.876,0) rot=(0,0,1;1.5708rad)
  LinkedObject = -> Shape
  Placement = pos=(-98.552,23.876,0) rot=(0,0,1;1.5708rad)
FEATURE [App::Link] J203_PinHeader_1x01_P254mm_Vertical_da6c4aed0287_ln_064  label="J149_PinHeader_1x01_P254mm_Vertical_3aa8ce42c7e0"
  LinkPlacement = pos=(-96.012,23.876,0) rot=(0,0,1;1.5708rad)
  LinkedObject = -> Shape
  Placement = pos=(-96.012,23.876,0) rot=(0,0,1;1.5708rad)
FEATURE [App::Link] LED2_FC_16_cp_sp120_3c06c14edb76_ln_  label="LED1_FC_16_cp_sp120_494d2cd2c793"
  LinkPlacement = pos=(0,-12.7,0) rot=(0,0,1;0rad)
  LinkedObject = -> FC_16_cp_sp
  Placement = pos=(0,-12.7,0) rot=(0,0,1;0rad)
FEATURE [App::Link] J203_PinHeader_1x01_P254mm_Vertical_da6c4aed0287_ln_065  label="J199_PinHeader_1x01_P254mm_Vertical_eca8f13e32ef"
  LinkPlacement = pos=(-125.476,19.558,0) rot=(0,0,1;1.5708rad)
  LinkedObject = -> Shape
  Placement = pos=(-125.476,19.558,0) rot=(0,0,1;1.5708rad)
FEATURE [App::Link] J203_PinHeader_1x01_P254mm_Vertical_da6c4aed0287_ln_066  label="J180_PinHeader_1x01_P254mm_Vertical_f90d0963c6ba"
  LinkPlacement = pos=(-135.636,27.178,0) rot=(0,0,1;1.5708rad)
  LinkedObject = -> Shape
  Placement = pos=(-135.636,27.178,0) rot=(0,0,1;1.5708rad)
FEATURE [App::Link] J203_PinHeader_1x01_P254mm_Vertical_da6c4aed0287_ln_067  label="J150_PinHeader_1x01_P254mm_Vertical_53a17cb67f8b"
  LinkPlacement = pos=(-106.172,21.336,0) rot=(0,0,1;1.5708rad)
  LinkedObject = -> Shape
  Placement = pos=(-106.172,21.336,0) rot=(0,0,1;1.5708rad)
FEATURE [App::Link] J203_PinHeader_1x01_P254mm_Vertical_da6c4aed0287_ln_068  label="J241_PinHeader_1x01_P254mm_Vertical_126f86256ea3"
  LinkPlacement = pos=(-86.614,23.368,0) rot=(0,0,1;1.5708rad)
  LinkedObject = -> Shape
  Placement = pos=(-86.614,23.368,0) rot=(0,0,1;1.5708rad)
FEATURE [App::Link] J203_PinHeader_1x01_P254mm_Vertical_da6c4aed0287_ln_069  label="J233_PinHeader_1x01_P254mm_Vertical_09f775719e70"
  LinkPlacement = pos=(-86.614,43.688,0) rot=(0,0,1;1.5708rad)
  LinkedObject = -> Shape
  Placement = pos=(-86.614,43.688,0) rot=(0,0,1;1.5708rad)
FEATURE [App::Link] J2_PinHeader_1x04_P254mm_Vertical_b8c18ff84878_ln_  label="J1_PinHeader_1x04_P254mm_Vertical_d596b9d5dcda"
  LinkPlacement = pos=(-26.67,-10.16,0) rot=(0,0,1;3.14159rad)
  LinkedObject = -> Shape002
  Placement = pos=(-26.67,-10.16,0) rot=(0,0,1;3.14159rad)
FEATURE [App::Link] J203_PinHeader_1x01_P254mm_Vertical_da6c4aed0287_ln_070  label="J179_PinHeader_1x01_P254mm_Vertical_7f8aaf0ebb89"
  LinkPlacement = pos=(-111.252,19.812,0) rot=(0,0,1;1.5708rad)
  LinkedObject = -> Shape
  Placement = pos=(-111.252,19.812,0) rot=(0,0,1;1.5708rad)
FEATURE [App::Link] J203_PinHeader_1x01_P254mm_Vertical_da6c4aed0287_ln_071  label="J152_PinHeader_1x01_P254mm_Vertical_82e8b89b00f4"
  LinkPlacement = pos=(-101.092,21.336,0) rot=(0,0,1;1.5708rad)
  LinkedObject = -> Shape
  Placement = pos=(-101.092,21.336,0) rot=(0,0,1;1.5708rad)
FEATURE [App::Link] J203_PinHeader_1x01_P254mm_Vertical_da6c4aed0287_ln_072  label="J196_PinHeader_1x01_P254mm_Vertical_dbeb0dc473ae"
  LinkPlacement = pos=(-133.096,19.558,0) rot=(0,0,1;1.5708rad)
  LinkedObject = -> Shape
  Placement = pos=(-133.096,19.558,0) rot=(0,0,1;1.5708rad)
FEATURE [App::Link] J203_PinHeader_1x01_P254mm_Vertical_da6c4aed0287_ln_073  label="J123_PinHeader_1x01_P254mm_Vertical_73db69d2a3e0"
  LinkPlacement = pos=(-98.552,36.576,0) rot=(0,0,1;1.5708rad)
  LinkedObject = -> Shape
  Placement = pos=(-98.552,36.576,0) rot=(0,0,1;1.5708rad)
FEATURE [App::Link] J203_PinHeader_1x01_P254mm_Vertical_da6c4aed0287_ln_074  label="J202_PinHeader_1x01_P254mm_Vertical_a7677ffdb21f"
  LinkPlacement = pos=(-145.796,27.686,0) rot=(0,0,1;1.5708rad)
  LinkedObject = -> Shape
  Placement = pos=(-145.796,27.686,0) rot=(0,0,1;1.5708rad)
FEATURE [App::Link] J203_PinHeader_1x01_P254mm_Vertical_da6c4aed0287_ln_075  label="J213_PinHeader_1x01_P254mm_Vertical_194bfab12c7b"
  LinkPlacement = pos=(-143.256,22.606,0) rot=(0,0,1;1.5708rad)
  LinkedObject = -> Shape
  Placement = pos=(-143.256,22.606,0) rot=(0,0,1;1.5708rad)
FEATURE [App::Link] J203_PinHeader_1x01_P254mm_Vertical_da6c4aed0287_ln_076  label="J132_PinHeader_1x01_P254mm_Vertical_025be7908b29"
  LinkPlacement = pos=(-101.092,31.496,0) rot=(0,0,1;1.5708rad)
  LinkedObject = -> Shape
  Placement = pos=(-101.092,31.496,0) rot=(0,0,1;1.5708rad)
FEATURE [App::Link] J203_PinHeader_1x01_P254mm_Vertical_da6c4aed0287_ln_077  label="J222_PinHeader_1x01_P254mm_Vertical_c664dcae36ff"
  LinkPlacement = pos=(-91.694,41.148,0) rot=(0,0,1;1.5708rad)
  LinkedObject = -> Shape
  Placement = pos=(-91.694,41.148,0) rot=(0,0,1;1.5708rad)
FEATURE [App::Link] J203_PinHeader_1x01_P254mm_Vertical_da6c4aed0287_ln_078  label="J209_PinHeader_1x01_P254mm_Vertical_4ecc4c67e1f5"
  LinkPlacement = pos=(-140.716,25.146,0) rot=(0,0,1;1.5708rad)
  LinkedObject = -> Shape
  Placement = pos=(-140.716,25.146,0) rot=(0,0,1;1.5708rad)
FEATURE [App::Link] J203_PinHeader_1x01_P254mm_Vertical_da6c4aed0287_ln_079  label="J115_PinHeader_1x01_P254mm_Vertical_40d9472fa62c"
  LinkPlacement = pos=(-106.172,39.116,0) rot=(0,0,1;1.5708rad)
  LinkedObject = -> Shape
  Placement = pos=(-106.172,39.116,0) rot=(0,0,1;1.5708rad)
FEATURE [App::Link] J203_PinHeader_1x01_P254mm_Vertical_da6c4aed0287_ln_080  label="J182_PinHeader_1x01_P254mm_Vertical_938da126562e"
  LinkPlacement = pos=(-130.556,27.178,0) rot=(0,0,1;1.5708rad)
  LinkedObject = -> Shape
  Placement = pos=(-130.556,27.178,0) rot=(0,0,1;1.5708rad)
FEATURE [App::Link] J203_PinHeader_1x01_P254mm_Vertical_da6c4aed0287_ln_081  label="J151_PinHeader_1x01_P254mm_Vertical_9f9c86e08493"
  LinkPlacement = pos=(-103.632,21.336,0) rot=(0,0,1;1.5708rad)
  LinkedObject = -> Shape
  Placement = pos=(-103.632,21.336,0) rot=(0,0,1;1.5708rad)
FEATURE [App::Link] J203_PinHeader_1x01_P254mm_Vertical_da6c4aed0287_ln_082  label="J121_PinHeader_1x01_P254mm_Vertical_3bc9cbe78fe7"
  LinkPlacement = pos=(-103.632,36.576,0) rot=(0,0,1;1.5708rad)
  LinkedObject = -> Shape
  Placement = pos=(-103.632,36.576,0) rot=(0,0,1;1.5708rad)
FEATURE [App::Link] J203_PinHeader_1x01_P254mm_Vertical_da6c4aed0287_ln_083  label="J162_PinHeader_1x01_P254mm_Vertical_d4bf07db4549"
  LinkPlacement = pos=(-116.332,27.432,0) rot=(0,0,1;1.5708rad)
  LinkedObject = -> Shape
  Placement = pos=(-116.332,27.432,0) rot=(0,0,1;1.5708rad)
FEATURE [App::Link] J203_PinHeader_1x01_P254mm_Vertical_da6c4aed0287_ln_084  label="J124_PinHeader_1x01_P254mm_Vertical_a57a65c5627e"
  LinkPlacement = pos=(-96.012,36.576,0) rot=(0,0,1;1.5708rad)
  LinkedObject = -> Shape
  Placement = pos=(-96.012,36.576,0) rot=(0,0,1;1.5708rad)
FEATURE [App::Link] J203_PinHeader_1x01_P254mm_Vertical_da6c4aed0287_ln_085  label="J105_PinHeader_1x01_P254mm_Vertical_0d5c741d8059"
  LinkPlacement = pos=(-106.172,44.196,0) rot=(0,0,1;1.5708rad)
  LinkedObject = -> Shape
  Placement = pos=(-106.172,44.196,0) rot=(0,0,1;1.5708rad)
FEATURE [App::Link] J203_PinHeader_1x01_P254mm_Vertical_da6c4aed0287_ln_086  label="J157_PinHeader_1x01_P254mm_Vertical_7500beba03ae"
  LinkPlacement = pos=(-101.092,18.796,0) rot=(0,0,1;1.5708rad)
  LinkedObject = -> Shape
  Placement = pos=(-101.092,18.796,0) rot=(0,0,1;1.5708rad)
FEATURE [App::Link] J203_PinHeader_1x01_P254mm_Vertical_da6c4aed0287_ln_087  label="J114_PinHeader_1x01_P254mm_Vertical_9c47f70119d7"
  LinkPlacement = pos=(-96.012,41.656,0) rot=(0,0,1;1.5708rad)
  LinkedObject = -> Shape
  Placement = pos=(-96.012,41.656,0) rot=(0,0,1;1.5708rad)
FEATURE [App::Link] J203_PinHeader_1x01_P254mm_Vertical_da6c4aed0287_ln_088  label="J110_PinHeader_1x01_P254mm_Vertical_7499e4b50451"
  LinkPlacement = pos=(-106.172,41.656,0) rot=(0,0,1;1.5708rad)
  LinkedObject = -> Shape
  Placement = pos=(-106.172,41.656,0) rot=(0,0,1;1.5708rad)
FEATURE [App::Link] J203_PinHeader_1x01_P254mm_Vertical_da6c4aed0287_ln_089  label="J130_PinHeader_1x01_P254mm_Vertical_7a9af1ba1e61"
  LinkPlacement = pos=(-106.172,31.496,0) rot=(0,0,1;1.5708rad)
  LinkedObject = -> Shape
  Placement = pos=(-106.172,31.496,0) rot=(0,0,1;1.5708rad)
FEATURE [App::Link] J203_PinHeader_1x01_P254mm_Vertical_da6c4aed0287_ln_090  label="J102_PinHeader_1x01_P254mm_Vertical_4abfdc338431"
  LinkPlacement = pos=(-101.092,46.736,0) rot=(0,0,1;1.5708rad)
  LinkedObject = -> Shape
  Placement = pos=(-101.092,46.736,0) rot=(0,0,1;1.5708rad)
FEATURE [App::Link] J203_PinHeader_1x01_P254mm_Vertical_da6c4aed0287_ln_091  label="J159_PinHeader_1x01_P254mm_Vertical_d819e2b56223"
  LinkPlacement = pos=(-96.012,18.796,0) rot=(0,0,1;1.5708rad)
  LinkedObject = -> Shape
  Placement = pos=(-96.012,18.796,0) rot=(0,0,1;1.5708rad)
FEATURE [App::Link] J203_PinHeader_1x01_P254mm_Vertical_da6c4aed0287_ln_092  label="J205_PinHeader_1x01_P254mm_Vertical_fb0fbb8af6ac"
  LinkPlacement = pos=(-150.876,25.146,0) rot=(0,0,1;1.5708rad)
  LinkedObject = -> Shape
  Placement = pos=(-150.876,25.146,0) rot=(0,0,1;1.5708rad)
FEATURE [App::Link] J203_PinHeader_1x01_P254mm_Vertical_da6c4aed0287_ln_093  label="J103_PinHeader_1x01_P254mm_Vertical_31a1e351a220"
  LinkPlacement = pos=(-98.552,46.736,0) rot=(0,0,1;1.5708rad)
  LinkedObject = -> Shape
  Placement = pos=(-98.552,46.736,0) rot=(0,0,1;1.5708rad)
FEATURE [App::Link] J203_PinHeader_1x01_P254mm_Vertical_da6c4aed0287_ln_094  label="J226_PinHeader_1x01_P254mm_Vertical_78c30bde38bb"
  LinkPlacement = pos=(-91.694,30.988,0) rot=(0,0,1;1.5708rad)
  LinkedObject = -> Shape
  Placement = pos=(-91.694,30.988,0) rot=(0,0,1;1.5708rad)
FEATURE [App::Link] J203_PinHeader_1x01_P254mm_Vertical_da6c4aed0287_ln_095  label="J240_PinHeader_1x01_P254mm_Vertical_54bc175320bf"
  LinkPlacement = pos=(-86.614,25.908,0) rot=(0,0,1;1.5708rad)
  LinkedObject = -> Shape
  Placement = pos=(-86.614,25.908,0) rot=(0,0,1;1.5708rad)
FEATURE [Part::Feature] Shape003  label="R2_R_Axial_DIN0207_L63mm_D25mm_P762mm_Horizontal_4ffd937b06bc"
  Placement = pos=(-26.67,-21.59,0) rot=(0,0,1;1.5708rad)
  shape: bbox 2.706 x 8.418 x 5.603 mm, 15 faces (baked)
FEATURE [App::Link] J203_PinHeader_1x01_P254mm_Vertical_da6c4aed0287_ln_096  label="J219_PinHeader_1x01_P254mm_Vertical_ebce06c72328"
  LinkPlacement = pos=(-140.716,20.066,0) rot=(0,0,1;1.5708rad)
  LinkedObject = -> Shape
  Placement = pos=(-140.716,20.066,0) rot=(0,0,1;1.5708rad)
FEATURE [App::Link] J203_PinHeader_1x01_P254mm_Vertical_da6c4aed0287_ln_097  label="J206_PinHeader_1x01_P254mm_Vertical_dc3c7c0b1a5e"
  LinkPlacement = pos=(-148.336,25.146,0) rot=(0,0,1;1.5708rad)
  LinkedObject = -> Shape
  Placement = pos=(-148.336,25.146,0) rot=(0,0,1;1.5708rad)
FEATURE [App::Link] J203_PinHeader_1x01_P254mm_Vertical_da6c4aed0287_ln_098  label="J101_PinHeader_1x01_P254mm_Vertical_d5addac4880f"
  LinkPlacement = pos=(-103.632,46.736,0) rot=(0,0,1;1.5708rad)
  LinkedObject = -> Shape
  Placement = pos=(-103.632,46.736,0) rot=(0,0,1;1.5708rad)
FEATURE [App::Link] J203_PinHeader_1x01_P254mm_Vertical_da6c4aed0287_ln_099  label="J171_PinHeader_1x01_P254mm_Vertical_57e33908ccdf"
  LinkPlacement = pos=(-118.872,22.352,0) rot=(0,0,1;1.5708rad)
  LinkedObject = -> Shape
  Placement = pos=(-118.872,22.352,0) rot=(0,0,1;1.5708rad)
FEATURE [App::Link] J203_PinHeader_1x01_P254mm_Vertical_da6c4aed0287_ln_100  label="J111_PinHeader_1x01_P254mm_Vertical_091943085e02"
  LinkPlacement = pos=(-103.632,41.656,0) rot=(0,0,1;1.5708rad)
  LinkedObject = -> Shape
  Placement = pos=(-103.632,41.656,0) rot=(0,0,1;1.5708rad)
FEATURE [App::Link] J203_PinHeader_1x01_P254mm_Vertical_da6c4aed0287_ln_101  label="J135_PinHeader_1x01_P254mm_Vertical_fce23acc187c"
  LinkPlacement = pos=(-106.172,28.956,0) rot=(0,0,1;1.5708rad)
  LinkedObject = -> Shape
  Placement = pos=(-106.172,28.956,0) rot=(0,0,1;1.5708rad)
FEATURE [App::Link] J203_PinHeader_1x01_P254mm_Vertical_da6c4aed0287_ln_102  label="J108_PinHeader_1x01_P254mm_Vertical_c615dfd59d0d"
  LinkPlacement = pos=(-98.552,44.196,0) rot=(0,0,1;1.5708rad)
  LinkedObject = -> Shape
  Placement = pos=(-98.552,44.196,0) rot=(0,0,1;1.5708rad)
FEATURE [App::Link] J203_PinHeader_1x01_P254mm_Vertical_da6c4aed0287_ln_103  label="J138_PinHeader_1x01_P254mm_Vertical_23b242c6379a"
  LinkPlacement = pos=(-98.552,28.956,0) rot=(0,0,1;1.5708rad)
  LinkedObject = -> Shape
  Placement = pos=(-98.552,28.956,0) rot=(0,0,1;1.5708rad)
FEATURE [App::Link] J203_PinHeader_1x01_P254mm_Vertical_da6c4aed0287_ln_104  label="J229_PinHeader_1x01_P254mm_Vertical_3e513ef12d77"
  LinkPlacement = pos=(-91.694,23.368,0) rot=(0,0,1;1.5708rad)
  LinkedObject = -> Shape
  Placement = pos=(-91.694,23.368,0) rot=(0,0,1;1.5708rad)
FEATURE [App::Link] J203_PinHeader_1x01_P254mm_Vertical_da6c4aed0287_ln_105  label="J170_PinHeader_1x01_P254mm_Vertical_f2e9ea1c82b0"
  LinkPlacement = pos=(-121.412,22.352,0) rot=(0,0,1;1.5708rad)
  LinkedObject = -> Shape
  Placement = pos=(-121.412,22.352,0) rot=(0,0,1;1.5708rad)
FEATURE [App::Link] J203_PinHeader_1x01_P254mm_Vertical_da6c4aed0287_ln_106  label="J211_PinHeader_1x01_P254mm_Vertical_43cc60315660"
  LinkPlacement = pos=(-148.336,22.606,0) rot=(0,0,1;1.5708rad)
  LinkedObject = -> Shape
  Placement = pos=(-148.336,22.606,0) rot=(0,0,1;1.5708rad)
FEATURE [App::Link] J203_PinHeader_1x01_P254mm_Vertical_da6c4aed0287_ln_107  label="J173_PinHeader_1x01_P254mm_Vertical_1208d51e8b5a"
  LinkPlacement = pos=(-113.792,22.352,0) rot=(0,0,1;1.5708rad)
  LinkedObject = -> Shape
  Placement = pos=(-113.792,22.352,0) rot=(0,0,1;1.5708rad)
FEATURE [App::Link] J203_PinHeader_1x01_P254mm_Vertical_da6c4aed0287_ln_108  label="J188_PinHeader_1x01_P254mm_Vertical_2c1d8ec06cea"
  LinkPlacement = pos=(-128.016,24.638,0) rot=(0,0,1;1.5708rad)
  LinkedObject = -> Shape
  Placement = pos=(-128.016,24.638,0) rot=(0,0,1;1.5708rad)
FEATURE [App::Link] J203_PinHeader_1x01_P254mm_Vertical_da6c4aed0287_ln_109  label="J217_PinHeader_1x01_P254mm_Vertical_a9f4566f65ae"
  LinkPlacement = pos=(-145.796,20.066,0) rot=(0,0,1;1.5708rad)
  LinkedObject = -> Shape
  Placement = pos=(-145.796,20.066,0) rot=(0,0,1;1.5708rad)
FEATURE [App::Link] J203_PinHeader_1x01_P254mm_Vertical_da6c4aed0287_ln_110  label="J106_PinHeader_1x01_P254mm_Vertical_b9e71965300f"
  LinkPlacement = pos=(-103.632,44.196,0) rot=(0,0,1;1.5708rad)
  LinkedObject = -> Shape
  Placement = pos=(-103.632,44.196,0) rot=(0,0,1;1.5708rad)
FEATURE [App::Link] J203_PinHeader_1x01_P254mm_Vertical_da6c4aed0287_ln_111  label="J189_PinHeader_1x01_P254mm_Vertical_273812b501d4"
  LinkPlacement = pos=(-125.476,24.638,0) rot=(0,0,1;1.5708rad)
  LinkedObject = -> Shape
  Placement = pos=(-125.476,24.638,0) rot=(0,0,1;1.5708rad)
FEATURE [App::Link] J203_PinHeader_1x01_P254mm_Vertical_da6c4aed0287_ln_112  label="J231_PinHeader_1x01_P254mm_Vertical_c66297164303"
  LinkPlacement = pos=(-91.694,18.288,0) rot=(0,0,1;1.5708rad)
  LinkedObject = -> Shape
  Placement = pos=(-91.694,18.288,0) rot=(0,0,1;1.5708rad)
FEATURE [App::Link] J203_PinHeader_1x01_P254mm_Vertical_da6c4aed0287_ln_113  label="J172_PinHeader_1x01_P254mm_Vertical_27413c652016"
  LinkPlacement = pos=(-116.332,22.352,0) rot=(0,0,1;1.5708rad)
  LinkedObject = -> Shape
  Placement = pos=(-116.332,22.352,0) rot=(0,0,1;1.5708rad)
FEATURE [App::Link] J203_PinHeader_1x01_P254mm_Vertical_da6c4aed0287_ln_114  label="J164_PinHeader_1x01_P254mm_Vertical_98c94443644b"
  LinkPlacement = pos=(-111.252,27.432,0) rot=(0,0,1;1.5708rad)
  LinkedObject = -> Shape
  Placement = pos=(-111.252,27.432,0) rot=(0,0,1;1.5708rad)
FEATURE [Part::Feature] Part__Feature129  label="arduino_nano_socket"
  shape: bbox 2.54 x 38.1 x 10.1 mm, 475 faces (baked)
FEATURE [Part::Feature] Part__Feature130  label="arduino_nano_socket001"
  shape: bbox 2.54 x 38.1 x 10.1 mm, 475 faces (baked)
FEATURE [Part::Feature] Part__Feature131  label="arduino_nano_socket002"
  shape: bbox 18 x 43.2 x 4.77 mm, 378 faces (baked)
FEATURE [Part::Feature] Part__Feature132  label="arduino_nano_socket003"
  shape: bbox 2.54 x 5 x 11.75 mm, 46 faces (baked)
FEATURE [Part::Feature] Part__Feature133  label="arduino_nano_socket004"
  shape: bbox 2.54 x 5 x 11.75 mm, 46 faces (baked)
FEATURE [Part::Feature] Part__Feature134  label="arduino_nano_socket005"
  shape: bbox 2.54 x 5 x 11.75 mm, 46 faces (baked)
FEATURE [Part::Feature] Part__Feature135  label="arduino_nano_socket006"
  shape: bbox 2.54 x 38.1 x 11.75 mm, 364 faces (baked)
FEATURE [Part::Feature] Part__Feature136  label="arduino_nano_socket007"
  shape: bbox 2.54 x 38.1 x 11.75 mm, 364 faces (baked)
FEATURE [Part::Feature] Part__Feature137  label="arduino_nano_socket008"
  shape: bbox 11.25 x 11.25 x 1.2 mm, 1867 faces (baked)
FEATURE [Part::Feature] Part__Feature138  label="arduino_nano_socket009"
  shape: bbox 9.287 x 10.2 x 1.9 mm, 717 faces (baked)
FEATURE [Part::Feature] Part__Feature139  label="arduino_nano_socket010"
  shape: bbox 1.813 x 3.8 x 0.6 mm, 74 faces (baked)
FEATURE [Part::Feature] Part__Feature140  label="arduino_nano_socket011"
  shape: bbox 1.813 x 3.8 x 0.6 mm, 74 faces (baked)
FEATURE [Part::Feature] Part__Feature141  label="arduino_nano_socket012"
  shape: bbox 1.813 x 3.8 x 0.6 mm, 74 faces (baked)
FEATURE [Part::Feature] Part__Feature142  label="arduino_nano_socket013"
  shape: bbox 1.813 x 3.8 x 0.6 mm, 74 faces (baked)
FEATURE [Part::Feature] Part__Feature143  label="arduino_nano_socket014"
  shape: bbox 1.813 x 3.8 x 0.6 mm, 74 faces (baked)
FEATURE [Part::Feature] Part__Feature144  label="arduino_nano_socket015"
  shape: bbox 2.138 x 4.438 x 0.5452 mm, 51 faces (baked)
FEATURE [Part::Feature] Part__Feature145  label="arduino_nano_socket016"
  shape: bbox 1.2 x 1.4 x 0.5 mm, 6 faces (baked)
FEATURE [Part::Feature] Part__Feature146  label="arduino_nano_socket017"
  shape: bbox 2.138 x 4.438 x 0.5452 mm, 51 faces (baked)
FEATURE [Part::Feature] Part__Feature147  label="arduino_nano_socket018"
  shape: bbox 1.2 x 1.4 x 0.5 mm, 6 faces (baked)
FEATURE [Part::Feature] Part__Feature148  label="arduino_nano_socket019"
  shape: bbox 2.138 x 4.438 x 0.5452 mm, 51 faces (baked)
FEATURE [Part::Feature] Part__Feature149  label="arduino_nano_socket020"
  shape: bbox 1.2 x 1.4 x 0.5 mm, 6 faces (baked)
FEATURE [Part::Feature] Part__Feature150  label="arduino_nano_socket021"
  shape: bbox 2.138 x 4.438 x 0.5452 mm, 51 faces (baked)
FEATURE [Part::Feature] Part__Feature151  label="arduino_nano_socket022"
  shape: bbox 1.2 x 1.4 x 0.5 mm, 6 faces (baked)
FEATURE [Part::Feature] Part__Feature152  label="arduino_nano_socket023"
  shape: bbox 3.394 x 3.394 x 0.8 mm, 71 faces (baked)
FEATURE [Part::Feature] Part__Feature153  label="arduino_nano_socket024"
  shape: bbox 11.03 x 9.475 x 3.822 mm, 243 faces (baked)
FEATURE [Part::Feature] Part__Feature154  label="arduino_nano_socket025"
  shape: bbox 7.7 x 8.2 x 4.5 mm, 127 faces (baked)
FEATURE [Part::Feature] Part__Feature155  label="arduino_nano_socket026"
  shape: bbox 0.5011 x 9.423 x 2.551 mm, 31 faces (baked)
FEATURE [Part::Feature] Part__Feature156  label="arduino_nano_socket027"
  shape: bbox 0.5011 x 9.423 x 2.551 mm, 31 faces (baked)
FEATURE [Part::Feature] Part__Feature157  label="arduino_nano_socket028"
  shape: bbox 0.5011 x 9.423 x 2.551 mm, 31 faces (baked)
FEATURE [Part::Feature] Part__Feature158  label="arduino_nano_socket029"
  shape: bbox 0.5011 x 9.423 x 2.551 mm, 31 faces (baked)
FEATURE [Part::Feature] Part__Feature159  label="arduino_nano_socket030"
  shape: bbox 0.5011 x 9.423 x 2.551 mm, 31 faces (baked)
FEATURE [Part::Feature] Part__Feature160  label="arduino_nano_socket031"
  shape: bbox 1.701 x 4.001 x 1.811 mm, 124 faces (baked)
FEATURE [Part::Feature] Part__Feature161  label="arduino_nano_socket032"
  shape: bbox 1.701 x 4.001 x 1.811 mm, 124 faces (baked)
FEATURE [Part::Feature] Part__Feature162  label="arduino_nano_socket033"
  shape: bbox 5.2 x 2.8 x 2.15 mm, 77 faces (baked)
FEATURE [Part::Feature] Part__Feature163  label="arduino_nano_socket034"
  shape: bbox 4 x 3 x 1.65 mm, 72 faces (baked)
FEATURE [Part::Feature] Part__Feature164  label="arduino_nano_socket035"
  shape: bbox 6.5 x 8.3 x 1.689 mm, 194 faces (baked)
FEATURE [Part::Feature] Part__Feature165  label="arduino_nano_socket036"
  shape: bbox 4.916 x 1.7 x 1.384 mm, 85 faces (baked)
FEATURE [Part::Feature] Part__Feature166  label="arduino_nano_socket037"
  shape: bbox 3.2 x 1.3 x 0.3 mm, 18 faces (baked)
FEATURE [Part::Feature] Part__Feature167  label="arduino_nano_socket038"
  shape: bbox 3.2 x 1.5 x 0.455 mm, 147 faces (baked)
FEATURE [Part::Feature] Part__Feature168  label="arduino_nano_socket039"
  shape: bbox 0.4001 x 0.9095 x 0.4736 mm, 15 faces (baked)
FEATURE [Part::Feature] Part__Feature169  label="arduino_nano_socket040"
  shape: bbox 0.4001 x 0.9095 x 0.4736 mm, 15 faces (baked)
FEATURE [Part::Feature] Part__Feature170  label="arduino_nano_socket041"
  shape: bbox 0.4001 x 0.9095 x 0.4736 mm, 15 faces (baked)
FEATURE [Part::Feature] Part__Feature171  label="arduino_nano_socket042"
  shape: bbox 0.4001 x 0.9095 x 0.4736 mm, 15 faces (baked)
FEATURE [Part::Feature] Part__Feature172  label="arduino_nano_socket043"
  shape: bbox 0.4001 x 0.9095 x 0.4736 mm, 15 faces (baked)
FEATURE [Part::Feature] Part__Feature173  label="arduino_nano_socket044"
  shape: bbox 0.4001 x 0.9095 x 0.4736 mm, 15 faces (baked)
FEATURE [Part::Feature] Part__Feature174  label="arduino_nano_socket045"
  shape: bbox 0.4001 x 0.9095 x 0.4736 mm, 15 faces (baked)
FEATURE [Part::Feature] Part__Feature175  label="arduino_nano_socket046"
  shape: bbox 0.4001 x 0.9095 x 0.4736 mm, 15 faces (baked)
FEATURE [Part::Feature] Part__Feature176  label="arduino_nano_socket047"
  shape: bbox 3.2 x 1.3 x 0.3 mm, 18 faces (baked)
FEATURE [Part::Feature] Part__Feature177  label="arduino_nano_socket048"
  shape: bbox 3.2 x 1.5 x 0.455 mm, 136 faces (baked)
FEATURE [Part::Feature] Part__Feature178  label="arduino_nano_socket049"
  shape: bbox 0.4001 x 0.9095 x 0.4736 mm, 15 faces (baked)
FEATURE [Part::Feature] Part__Feature179  label="arduino_nano_socket050"
  shape: bbox 0.4001 x 0.9095 x 0.4736 mm, 15 faces (baked)
FEATURE [Part::Feature] Part__Feature180  label="arduino_nano_socket051"
  shape: bbox 0.4001 x 0.9095 x 0.4736 mm, 15 faces (baked)
FEATURE [Part::Feature] Part__Feature181  label="arduino_nano_socket052"
  shape: bbox 0.4001 x 0.9095 x 0.4736 mm, 15 faces (baked)
FEATURE [Part::Feature] Part__Feature182  label="arduino_nano_socket053"
  shape: bbox 0.4001 x 0.9095 x 0.4736 mm, 15 faces (baked)
FEATURE [Part::Feature] Part__Feature183  label="arduino_nano_socket054"
  shape: bbox 0.4001 x 0.9095 x 0.4736 mm, 15 faces (baked)
FEATURE [Part::Feature] Part__Feature184  label="arduino_nano_socket055"
  shape: bbox 0.4001 x 0.9095 x 0.4736 mm, 15 faces (baked)
FEATURE [Part::Feature] Part__Feature185  label="arduino_nano_socket056"
  shape: bbox 0.4001 x 0.9095 x 0.4736 mm, 15 faces (baked)
FEATURE [App::Part] arduino_nano_socket  label="U1_arduino_nano_socket057_d5ff97aaa247"
  Group = -> [Part__Feature129,Part__Feature130,Part__Feature131,Part__Feature132,Part__Feature133,Part__Feature134,Part__Feature135,Part__Feature136,Part__Feature137,Part__Feature138,Part__Feature139,Part__Feature140,Part__Feature141,Part__Feature142,Part__Feature143,Part__Feature144,Part__Feature145,Part__Feature146,Part__Feature147,Part__Feature148,Part__Feature149,Part__Feature150,Part__Feature151,+34 more]
  Origin = -> Origin010
  Placement = pos=(20.32,12.7,0) rot=(0,0,-1;1.5708rad)
FEATURE [App::Link] J203_PinHeader_1x01_P254mm_Vertical_da6c4aed0287_ln_115  label="J122_PinHeader_1x01_P254mm_Vertical_3719b8bfbef6"
  LinkPlacement = pos=(-101.092,36.576,0) rot=(0,0,1;1.5708rad)
  LinkedObject = -> Shape
  Placement = pos=(-101.092,36.576,0) rot=(0,0,1;1.5708rad)
FEATURE [App::Link] J203_PinHeader_1x01_P254mm_Vertical_da6c4aed0287_ln_116  label="J194_PinHeader_1x01_P254mm_Vertical_8bbe0a156270"
  LinkPlacement = pos=(-125.476,22.098,0) rot=(0,0,1;1.5708rad)
  LinkedObject = -> Shape
  Placement = pos=(-125.476,22.098,0) rot=(0,0,1;1.5708rad)
FEATURE [App::Link] J203_PinHeader_1x01_P254mm_Vertical_da6c4aed0287_ln_117  label="J107_PinHeader_1x01_P254mm_Vertical_834a8c7ff8ec"
  LinkPlacement = pos=(-101.092,44.196,0) rot=(0,0,1;1.5708rad)
  LinkedObject = -> Shape
  Placement = pos=(-101.092,44.196,0) rot=(0,0,1;1.5708rad)
FEATURE [App::Link] J203_PinHeader_1x01_P254mm_Vertical_da6c4aed0287_ln_118  label="J165_PinHeader_1x01_P254mm_Vertical_19fd1eed3c14"
  LinkPlacement = pos=(-121.412,24.892,0) rot=(0,0,1;1.5708rad)
  LinkedObject = -> Shape
  Placement = pos=(-121.412,24.892,0) rot=(0,0,1;1.5708rad)
FEATURE [App::Link] J203_PinHeader_1x01_P254mm_Vertical_da6c4aed0287_ln_119  label="J116_PinHeader_1x01_P254mm_Vertical_9c303331918c"
  LinkPlacement = pos=(-103.632,39.116,0) rot=(0,0,1;1.5708rad)
  LinkedObject = -> Shape
  Placement = pos=(-103.632,39.116,0) rot=(0,0,1;1.5708rad)
FEATURE [App::Link] J203_PinHeader_1x01_P254mm_Vertical_da6c4aed0287_ln_120  label="J178_PinHeader_1x01_P254mm_Vertical_8f00b17ca227"
  LinkPlacement = pos=(-113.792,19.812,0) rot=(0,0,1;1.5708rad)
  LinkedObject = -> Shape
  Placement = pos=(-113.792,19.812,0) rot=(0,0,1;1.5708rad)
FEATURE [Part::Feature] Shape004  label="SW1_1_219a87e7a09f"
  Placement = pos=(-15.05,25.94,0) rot=(0,0,1;3.14159rad)
  shape: bbox 8.6 x 8.4 x 7.6 mm, 200 faces (baked)
FEATURE [App::Link] J203_PinHeader_1x01_P254mm_Vertical_da6c4aed0287_ln_121  label="J218_PinHeader_1x01_P254mm_Vertical_ddb246e2b68f"
  LinkPlacement = pos=(-143.256,20.066,0) rot=(0,0,1;1.5708rad)
  LinkedObject = -> Shape
  Placement = pos=(-143.256,20.066,0) rot=(0,0,1;1.5708rad)
FEATURE [App::Link] J203_PinHeader_1x01_P254mm_Vertical_da6c4aed0287_ln_122  label="J131_PinHeader_1x01_P254mm_Vertical_6f7223393ee7"
  LinkPlacement = pos=(-103.632,31.496,0) rot=(0,0,1;1.5708rad)
  LinkedObject = -> Shape
  Placement = pos=(-103.632,31.496,0) rot=(0,0,1;1.5708rad)
FEATURE [App::Link] J203_PinHeader_1x01_P254mm_Vertical_da6c4aed0287_ln_123  label="J237_PinHeader_1x01_P254mm_Vertical_5f4b7ee06fb6"
  LinkPlacement = pos=(-86.614,33.528,0) rot=(0,0,1;1.5708rad)
  LinkedObject = -> Shape
  Placement = pos=(-86.614,33.528,0) rot=(0,0,1;1.5708rad)
FEATURE [App::Link] J203_PinHeader_1x01_P254mm_Vertical_da6c4aed0287_ln_124  label="J176_PinHeader_1x01_P254mm_Vertical_4000ad0be508"
  LinkPlacement = pos=(-118.872,19.812,0) rot=(0,0,1;1.5708rad)
  LinkedObject = -> Shape
  Placement = pos=(-118.872,19.812,0) rot=(0,0,1;1.5708rad)
FEATURE [App::Link] J203_PinHeader_1x01_P254mm_Vertical_da6c4aed0287_ln_125  label="J223_PinHeader_1x01_P254mm_Vertical_715095ab3421"
  LinkPlacement = pos=(-91.694,38.608,0) rot=(0,0,1;1.5708rad)
  LinkedObject = -> Shape
  Placement = pos=(-91.694,38.608,0) rot=(0,0,1;1.5708rad)
FEATURE [App::Link] J203_PinHeader_1x01_P254mm_Vertical_da6c4aed0287_ln_126  label="J169_PinHeader_1x01_P254mm_Vertical_7f03a88063f0"
  LinkPlacement = pos=(-111.252,24.892,0) rot=(0,0,1;1.5708rad)
  LinkedObject = -> Shape
  Placement = pos=(-111.252,24.892,0) rot=(0,0,1;1.5708rad)
FEATURE [App::Link] J203_PinHeader_1x01_P254mm_Vertical_da6c4aed0287_ln_127  label="J243_PinHeader_1x01_P254mm_Vertical_c20925e9c58a"
  LinkPlacement = pos=(-86.614,18.288,0) rot=(0,0,1;1.5708rad)
  LinkedObject = -> Shape
  Placement = pos=(-86.614,18.288,0) rot=(0,0,1;1.5708rad)
FEATURE [App::Link] J203_PinHeader_1x01_P254mm_Vertical_da6c4aed0287_ln_128  label="J143_PinHeader_1x01_P254mm_Vertical_5c27870e4a0a"
  LinkPlacement = pos=(-98.552,26.416,0) rot=(0,0,1;1.5708rad)
  LinkedObject = -> Shape
  Placement = pos=(-98.552,26.416,0) rot=(0,0,1;1.5708rad)
FEATURE [App::Link] J203_PinHeader_1x01_P254mm_Vertical_da6c4aed0287_ln_129  label="J224_PinHeader_1x01_P254mm_Vertical_eb59192aacbb"
  LinkPlacement = pos=(-91.694,36.068,0) rot=(0,0,1;1.5708rad)
  LinkedObject = -> Shape
  Placement = pos=(-91.694,36.068,0) rot=(0,0,1;1.5708rad)
FEATURE [App::Link] J203_PinHeader_1x01_P254mm_Vertical_da6c4aed0287_ln_130  label="J133_PinHeader_1x01_P254mm_Vertical_97dac205dec5"
  LinkPlacement = pos=(-98.552,31.496,0) rot=(0,0,1;1.5708rad)
  LinkedObject = -> Shape
  Placement = pos=(-98.552,31.496,0) rot=(0,0,1;1.5708rad)
FEATURE [App::Link] J203_PinHeader_1x01_P254mm_Vertical_da6c4aed0287_ln_131  label="J200_PinHeader_1x01_P254mm_Vertical_bcae4cc085b8"
  LinkPlacement = pos=(-150.876,27.686,0) rot=(0,0,1;1.5708rad)
  LinkedObject = -> Shape
  Placement = pos=(-150.876,27.686,0) rot=(0,0,1;1.5708rad)
FEATURE [App::Link] J203_PinHeader_1x01_P254mm_Vertical_da6c4aed0287_ln_132  label="J144_PinHeader_1x01_P254mm_Vertical_365826054727"
  LinkPlacement = pos=(-96.012,26.416,0) rot=(0,0,1;1.5708rad)
  LinkedObject = -> Shape
  Placement = pos=(-96.012,26.416,0) rot=(0,0,1;1.5708rad)
FEATURE [App::Link] J203_PinHeader_1x01_P254mm_Vertical_da6c4aed0287_ln_133  label="J147_PinHeader_1x01_P254mm_Vertical_63aea639777b"
  LinkPlacement = pos=(-101.092,23.876,0) rot=(0,0,1;1.5708rad)
  LinkedObject = -> Shape
  Placement = pos=(-101.092,23.876,0) rot=(0,0,1;1.5708rad)
FEATURE [App::Link] J203_PinHeader_1x01_P254mm_Vertical_da6c4aed0287_ln_134  label="J183_PinHeader_1x01_P254mm_Vertical_39be94face5b"
  LinkPlacement = pos=(-128.016,27.178,0) rot=(0,0,1;1.5708rad)
  LinkedObject = -> Shape
  Placement = pos=(-128.016,27.178,0) rot=(0,0,1;1.5708rad)
FEATURE [App::Link] J203_PinHeader_1x01_P254mm_Vertical_da6c4aed0287_ln_135  label="J228_PinHeader_1x01_P254mm_Vertical_ac9689348f1e"
  LinkPlacement = pos=(-91.694,25.908,0) rot=(0,0,1;1.5708rad)
  LinkedObject = -> Shape
  Placement = pos=(-91.694,25.908,0) rot=(0,0,1;1.5708rad)
FEATURE [Part::Feature] Shape005  label="D1_D_DO-41_SOD81_P10.16mm_Horizontal_32ec51f60e8f"
  Placement = pos=(10.16,27.94,0) rot=(0,0,1;0rad)
  shape: bbox 11.16 x 2.72 x 5.71 mm, 15 faces (baked)
FEATURE [App::Link] R2_R_Axial_DIN0207_L63mm_D25mm_P762mm_Horizontal_4ffd937b06bc_ln_  label="R1_R_Axial_DIN0207_L63mm_D25mm_P762mm_Horizontal_6afa1d7f9f45"
  LinkPlacement = pos=(-22.86,-21.59,0) rot=(0,0,1;1.5708rad)
  LinkedObject = -> Shape003
  Placement = pos=(-22.86,-21.59,0) rot=(0,0,1;1.5708rad)
FEATURE [App::Link] J203_PinHeader_1x01_P254mm_Vertical_da6c4aed0287_ln_136  label="J140_PinHeader_1x01_P254mm_Vertical_fd6252600da0"
  LinkPlacement = pos=(-106.172,26.416,0) rot=(0,0,1;1.5708rad)
  LinkedObject = -> Shape
  Placement = pos=(-106.172,26.416,0) rot=(0,0,1;1.5708rad)
FEATURE [App::Link] J203_PinHeader_1x01_P254mm_Vertical_da6c4aed0287_ln_137  label="J220_PinHeader_1x01_P254mm_Vertical_2b513a9ba3c4"
  LinkPlacement = pos=(-91.694,46.228,0) rot=(0,0,1;1.5708rad)
  LinkedObject = -> Shape
  Placement = pos=(-91.694,46.228,0) rot=(0,0,1;1.5708rad)
FEATURE [App::Link] J203_PinHeader_1x01_P254mm_Vertical_da6c4aed0287_ln_138  label="J227_PinHeader_1x01_P254mm_Vertical_4c40cb5d0a31"
  LinkPlacement = pos=(-91.694,28.448,0) rot=(0,0,1;1.5708rad)
  LinkedObject = -> Shape
  Placement = pos=(-91.694,28.448,0) rot=(0,0,1;1.5708rad)
FEATURE [App::Link] J203_PinHeader_1x01_P254mm_Vertical_da6c4aed0287_ln_139  label="J100_PinHeader_1x01_P254mm_Vertical_75ac60a93074"
  LinkPlacement = pos=(-106.172,46.736,0) rot=(0,0,1;1.5708rad)
  LinkedObject = -> Shape
  Placement = pos=(-106.172,46.736,0) rot=(0,0,1;1.5708rad)
FEATURE [App::Link] J203_PinHeader_1x01_P254mm_Vertical_da6c4aed0287_ln_140  label="J236_PinHeader_1x01_P254mm_Vertical_62cb4bf3d7c4"
  LinkPlacement = pos=(-86.614,36.068,0) rot=(0,0,1;1.5708rad)
  LinkedObject = -> Shape
  Placement = pos=(-86.614,36.068,0) rot=(0,0,1;1.5708rad)
FEATURE [App::Link] J203_PinHeader_1x01_P254mm_Vertical_da6c4aed0287_ln_141  label="J225_PinHeader_1x01_P254mm_Vertical_6b683ad1e7c4"
  LinkPlacement = pos=(-91.694,33.528,0) rot=(0,0,1;1.5708rad)
  LinkedObject = -> Shape
  Placement = pos=(-91.694,33.528,0) rot=(0,0,1;1.5708rad)
FEATURE [App::Link] J203_PinHeader_1x01_P254mm_Vertical_da6c4aed0287_ln_142  label="J230_PinHeader_1x01_P254mm_Vertical_a42af108c35d"
  LinkPlacement = pos=(-91.694,20.828,0) rot=(0,0,1;1.5708rad)
  LinkedObject = -> Shape
  Placement = pos=(-91.694,20.828,0) rot=(0,0,1;1.5708rad)
FEATURE [App::Part] Top_fc76
  Group = -> [Shape,J203_PinHeader_1x01_P254mm_Vertical_da6c4aed0287_ln_,J203_PinHeader_1x01_P254mm_Vertical_da6c4aed0287_ln_001,J203_PinHeader_1x01_P254mm_Vertical_da6c4aed0287_ln_002,J203_PinHeader_1x01_P254mm_Vertical_da6c4aed0287_ln_003,J203_PinHeader_1x01_P254mm_Vertical_da6c4aed0287_ln_004,J203_PinHeader_1x01_P254mm_Vertical_da6c4aed0287_ln_005,J203_PinHeader_1x01_P254mm_Vertical_da6c4aed0287_ln_006,+147 more]
  Origin = -> Origin003
FEATURE [App::Link] J203_PinHeader_1x01_P254mm_Vertical_da6c4aed0287_ln_143  label="J10_PinHeader_1x01_P254mm_Vertical_c9b2285a6f13"
  LinkPlacement = pos=(7.62,17.78,-1.6) rot=(0.707107,0.707107,0;3.14159rad)
  LinkedObject = -> Shape
  Placement = pos=(7.62,17.78,-1.6) rot=(0.707107,0.707107,0;3.14159rad)
FEATURE [App::Link] J203_PinHeader_1x01_P254mm_Vertical_da6c4aed0287_ln_144  label="J25_PinHeader_1x01_P254mm_Vertical_b3db6972f96f"
  LinkPlacement = pos=(17.78,17.78,-1.6) rot=(0.707107,0.707107,0;3.14159rad)
  LinkedObject = -> Shape
  Placement = pos=(17.78,17.78,-1.6) rot=(0.707107,0.707107,0;3.14159rad)
FEATURE [App::Link] J203_PinHeader_1x01_P254mm_Vertical_da6c4aed0287_ln_145  label="J18_PinHeader_1x01_P254mm_Vertical_bf699268af4c"
  LinkPlacement = pos=(-12.7,17.78,-1.6) rot=(0.707107,0.707107,0;3.14159rad)
  LinkedObject = -> Shape
  Placement = pos=(-12.7,17.78,-1.6) rot=(0.707107,0.707107,0;3.14159rad)
FEATURE [App::Link] J203_PinHeader_1x01_P254mm_Vertical_da6c4aed0287_ln_146  label="J35_PinHeader_1x01_P254mm_Vertical_58b75af8ef85"
  LinkPlacement = pos=(17.78,7.62,-1.6) rot=(0.707107,0.707107,0;3.14159rad)
  LinkedObject = -> Shape
  Placement = pos=(17.78,7.62,-1.6) rot=(0.707107,0.707107,0;3.14159rad)
FEATURE [App::Link] J203_PinHeader_1x01_P254mm_Vertical_da6c4aed0287_ln_147  label="J32_PinHeader_1x01_P254mm_Vertical_b4f680f1af2d"
  LinkPlacement = pos=(-7.62,7.62,-1.6) rot=(0.707107,0.707107,0;3.14159rad)
  LinkedObject = -> Shape
  Placement = pos=(-7.62,7.62,-1.6) rot=(0.707107,0.707107,0;3.14159rad)
FEATURE [App::Link] J203_PinHeader_1x01_P254mm_Vertical_da6c4aed0287_ln_148  label="J24_PinHeader_1x01_P254mm_Vertical_e98a18c1f6ef"
  LinkPlacement = pos=(15.24,17.78,-1.6) rot=(0.707107,0.707107,0;3.14159rad)
  LinkedObject = -> Shape
  Placement = pos=(15.24,17.78,-1.6) rot=(0.707107,0.707107,0;3.14159rad)
FEATURE [App::Link] J203_PinHeader_1x01_P254mm_Vertical_da6c4aed0287_ln_149  label="J13_PinHeader_1x01_P254mm_Vertical_cd3758c55ec9"
  LinkPlacement = pos=(2e-16,17.78,-1.6) rot=(0.707107,0.707107,0;3.14159rad)
  LinkedObject = -> Shape
  Placement = pos=(2e-16,17.78,-1.6) rot=(0.707107,0.707107,0;3.14159rad)
FEATURE [App::Link] J203_PinHeader_1x01_P254mm_Vertical_da6c4aed0287_ln_150  label="J20_PinHeader_1x01_P254mm_Vertical_9e959caa93af"
  LinkPlacement = pos=(-17.78,17.78,-1.6) rot=(0.707107,0.707107,0;3.14159rad)
  LinkedObject = -> Shape
  Placement = pos=(-17.78,17.78,-1.6) rot=(0.707107,0.707107,0;3.14159rad)
FEATURE [App::Link] J203_PinHeader_1x01_P254mm_Vertical_da6c4aed0287_ln_151  label="J11_PinHeader_1x01_P254mm_Vertical_85c80b18d1db"
  LinkPlacement = pos=(5.08,17.78,-1.6) rot=(0.707107,0.707107,0;3.14159rad)
  LinkedObject = -> Shape
  Placement = pos=(5.08,17.78,-1.6) rot=(0.707107,0.707107,0;3.14159rad)
FEATURE [App::Link] J203_PinHeader_1x01_P254mm_Vertical_da6c4aed0287_ln_152  label="J22_PinHeader_1x01_P254mm_Vertical_bf06523fea07"
  LinkPlacement = pos=(12.7,17.78,-1.6) rot=(0.707107,0.707107,0;3.14159rad)
  LinkedObject = -> Shape
  Placement = pos=(12.7,17.78,-1.6) rot=(0.707107,0.707107,0;3.14159rad)
FEATURE [App::Link] J203_PinHeader_1x01_P254mm_Vertical_da6c4aed0287_ln_153  label="J39_PinHeader_1x01_P254mm_Vertical_ee7d523646c7"
  LinkPlacement = pos=(10.16,17.78,-1.6) rot=(0.707107,0.707107,0;3.14159rad)
  LinkedObject = -> Shape
  Placement = pos=(10.16,17.78,-1.6) rot=(0.707107,0.707107,0;3.14159rad)
FEATURE [App::Link] J203_PinHeader_1x01_P254mm_Vertical_da6c4aed0287_ln_154  label="J36_PinHeader_1x01_P254mm_Vertical_d89022d6458d"
  LinkPlacement = pos=(10.16,7.62,-1.6) rot=(0.707107,0.707107,0;3.14159rad)
  LinkedObject = -> Shape
  Placement = pos=(10.16,7.62,-1.6) rot=(0.707107,0.707107,0;3.14159rad)
FEATURE [App::Link] J203_PinHeader_1x01_P254mm_Vertical_da6c4aed0287_ln_155  label="J21_PinHeader_1x01_P254mm_Vertical_f9c51dc1377b"
  LinkPlacement = pos=(-17.78,7.62,-1.6) rot=(0.707107,0.707107,0;3.14159rad)
  LinkedObject = -> Shape
  Placement = pos=(-17.78,7.62,-1.6) rot=(0.707107,0.707107,0;3.14159rad)
FEATURE [App::Link] J203_PinHeader_1x01_P254mm_Vertical_da6c4aed0287_ln_156  label="J26_PinHeader_1x01_P254mm_Vertical_99255f430fe9"
  LinkPlacement = pos=(7.62,7.62,-1.6) rot=(0.707107,0.707107,0;3.14159rad)
  LinkedObject = -> Shape
  Placement = pos=(7.62,7.62,-1.6) rot=(0.707107,0.707107,0;3.14159rad)
FEATURE [App::Link] J203_PinHeader_1x01_P254mm_Vertical_da6c4aed0287_ln_157  label="J34_PinHeader_1x01_P254mm_Vertical_4232218274a7"
  LinkPlacement = pos=(-12.7,7.62,-1.6) rot=(0.707107,0.707107,0;3.14159rad)
  LinkedObject = -> Shape
  Placement = pos=(-12.7,7.62,-1.6) rot=(0.707107,0.707107,0;3.14159rad)
FEATURE [App::Link] J203_PinHeader_1x01_P254mm_Vertical_da6c4aed0287_ln_158  label="J29_PinHeader_1x01_P254mm_Vertical_694e1429e0a8"
  LinkPlacement = pos=(2e-16,7.62,-1.6) rot=(0.707107,0.707107,0;3.14159rad)
  LinkedObject = -> Shape
  Placement = pos=(2e-16,7.62,-1.6) rot=(0.707107,0.707107,0;3.14159rad)
FEATURE [App::Link] J203_PinHeader_1x01_P254mm_Vertical_da6c4aed0287_ln_159  label="J17_PinHeader_1x01_P254mm_Vertical_8c962275048e"
  LinkPlacement = pos=(-10.16,17.78,-1.6) rot=(0.707107,0.707107,0;3.14159rad)
  LinkedObject = -> Shape
  Placement = pos=(-10.16,17.78,-1.6) rot=(0.707107,0.707107,0;3.14159rad)
FEATURE [App::Link] J203_PinHeader_1x01_P254mm_Vertical_da6c4aed0287_ln_160  label="J12_PinHeader_1x01_P254mm_Vertical_e79b290a1b2f"
  LinkPlacement = pos=(2.54,17.78,-1.6) rot=(0.707107,0.707107,0;3.14159rad)
  LinkedObject = -> Shape
  Placement = pos=(2.54,17.78,-1.6) rot=(0.707107,0.707107,0;3.14159rad)
FEATURE [App::Link] J203_PinHeader_1x01_P254mm_Vertical_da6c4aed0287_ln_161  label="J23_PinHeader_1x01_P254mm_Vertical_19fd117b2d81"
  LinkPlacement = pos=(12.7,7.62,-1.6) rot=(0.707107,0.707107,0;3.14159rad)
  LinkedObject = -> Shape
  Placement = pos=(12.7,7.62,-1.6) rot=(0.707107,0.707107,0;3.14159rad)
FEATURE [App::Link] J203_PinHeader_1x01_P254mm_Vertical_da6c4aed0287_ln_162  label="J16_PinHeader_1x01_P254mm_Vertical_a6037da68925"
  LinkPlacement = pos=(-7.62,17.78,-1.6) rot=(0.707107,0.707107,0;3.14159rad)
  LinkedObject = -> Shape
  Placement = pos=(-7.62,17.78,-1.6) rot=(0.707107,0.707107,0;3.14159rad)
FEATURE [App::Link] J203_PinHeader_1x01_P254mm_Vertical_da6c4aed0287_ln_163  label="J38_PinHeader_1x01_P254mm_Vertical_a07f460d1739"
  LinkPlacement = pos=(15.24,7.62,-1.6) rot=(0.707107,0.707107,0;3.14159rad)
  LinkedObject = -> Shape
  Placement = pos=(15.24,7.62,-1.6) rot=(0.707107,0.707107,0;3.14159rad)
FEATURE [App::Link] J203_PinHeader_1x01_P254mm_Vertical_da6c4aed0287_ln_164  label="J33_PinHeader_1x01_P254mm_Vertical_521704952a7b"
  LinkPlacement = pos=(-10.16,7.62,-1.6) rot=(0.707107,0.707107,0;3.14159rad)
  LinkedObject = -> Shape
  Placement = pos=(-10.16,7.62,-1.6) rot=(0.707107,0.707107,0;3.14159rad)
FEATURE [App::Link] J203_PinHeader_1x01_P254mm_Vertical_da6c4aed0287_ln_165  label="J27_PinHeader_1x01_P254mm_Vertical_f62cfaf39179"
  LinkPlacement = pos=(5.08,7.62,-1.6) rot=(0.707107,0.707107,0;3.14159rad)
  LinkedObject = -> Shape
  Placement = pos=(5.08,7.62,-1.6) rot=(0.707107,0.707107,0;3.14159rad)
FEATURE [App::Link] J203_PinHeader_1x01_P254mm_Vertical_da6c4aed0287_ln_166  label="J37_PinHeader_1x01_P254mm_Vertical_e15f19f11d9b"
  LinkPlacement = pos=(-15.24,7.62,-1.6) rot=(0.707107,0.707107,0;3.14159rad)
  LinkedObject = -> Shape
  Placement = pos=(-15.24,7.62,-1.6) rot=(0.707107,0.707107,0;3.14159rad)
FEATURE [App::Link] J203_PinHeader_1x01_P254mm_Vertical_da6c4aed0287_ln_167  label="J30_PinHeader_1x01_P254mm_Vertical_243e8eef6838"
  LinkPlacement = pos=(-2.54,7.62,-1.6) rot=(0.707107,0.707107,0;3.14159rad)
  LinkedObject = -> Shape
  Placement = pos=(-2.54,7.62,-1.6) rot=(0.707107,0.707107,0;3.14159rad)
FEATURE [App::Link] J203_PinHeader_1x01_P254mm_Vertical_da6c4aed0287_ln_168  label="J15_PinHeader_1x01_P254mm_Vertical_3593996b4a22"
  LinkPlacement = pos=(-5.08,17.78,-1.6) rot=(0.707107,0.707107,0;3.14159rad)
  LinkedObject = -> Shape
  Placement = pos=(-5.08,17.78,-1.6) rot=(0.707107,0.707107,0;3.14159rad)
FEATURE [App::Link] J203_PinHeader_1x01_P254mm_Vertical_da6c4aed0287_ln_169  label="J28_PinHeader_1x01_P254mm_Vertical_9b5adb342cd1"
  LinkPlacement = pos=(2.54,7.62,-1.6) rot=(0.707107,0.707107,0;3.14159rad)
  LinkedObject = -> Shape
  Placement = pos=(2.54,7.62,-1.6) rot=(0.707107,0.707107,0;3.14159rad)
FEATURE [App::Link] J203_PinHeader_1x01_P254mm_Vertical_da6c4aed0287_ln_170  label="J31_PinHeader_1x01_P254mm_Vertical_aefb021bfb32"
  LinkPlacement = pos=(-5.08,7.62,-1.6) rot=(0.707107,0.707107,0;3.14159rad)
  LinkedObject = -> Shape
  Placement = pos=(-5.08,7.62,-1.6) rot=(0.707107,0.707107,0;3.14159rad)
FEATURE [App::Link] J203_PinHeader_1x01_P254mm_Vertical_da6c4aed0287_ln_171  label="J14_PinHeader_1x01_P254mm_Vertical_5fa077225f2d"
  LinkPlacement = pos=(-2.54,17.78,-1.6) rot=(0.707107,0.707107,0;3.14159rad)
  LinkedObject = -> Shape
  Placement = pos=(-2.54,17.78,-1.6) rot=(0.707107,0.707107,0;3.14159rad)
FEATURE [App::Link] J203_PinHeader_1x01_P254mm_Vertical_da6c4aed0287_ln_172  label="J19_PinHeader_1x01_P254mm_Vertical_3d1c2f6a0c8f"
  LinkPlacement = pos=(-15.24,17.78,-1.6) rot=(0.707107,0.707107,0;3.14159rad)
  LinkedObject = -> Shape
  Placement = pos=(-15.24,17.78,-1.6) rot=(0.707107,0.707107,0;3.14159rad)
FEATURE [App::Part] Bot_fc76
  Group = -> [J203_PinHeader_1x01_P254mm_Vertical_da6c4aed0287_ln_143,J203_PinHeader_1x01_P254mm_Vertical_da6c4aed0287_ln_144,J203_PinHeader_1x01_P254mm_Vertical_da6c4aed0287_ln_145,J203_PinHeader_1x01_P254mm_Vertical_da6c4aed0287_ln_146,J203_PinHeader_1x01_P254mm_Vertical_da6c4aed0287_ln_147,J203_PinHeader_1x01_P254mm_Vertical_da6c4aed0287_ln_148,J203_PinHeader_1x01_P254mm_Vertical_da6c4aed0287_ln_149,+23 more]
  Origin = -> Origin004
FEATURE [App::Part] Step_Models_fc76
  Group = -> [Top_fc76,Bot_fc76]
  Origin = -> Origin002
FEATURE [App::Part] Board_fc76  label="BagTag"
  Group = -> [Local_CS_fc76,Board_Geoms_fc76,Step_Models_fc76]
  Origin = -> Origin001
FEATURE [Part::Feature] Part__Feature186  label="pp3_battery009"
  shape: bbox 1.5 x 6.35 x 6.35 mm, 3 faces, 0 solids (baked)
FEATURE [Part::Feature] Part__Feature187  label="pp3_battery010"
  shape: bbox 42.82 x 26 x 16.6 mm, 196 faces, 0 solids (baked)
FEATURE [Part::Feature] Part__Feature188  label="pp3_battery011"
  shape: bbox 3.2 x 8 x 8 mm, 11 faces, 0 solids (baked)
FEATURE [Part::Feature] Part__Feature189  label="pp3_battery012"
  shape: bbox 0.0001965 x 6.345 x 2.963e-07 mm, 1 faces, 0 solids (baked)
FEATURE [Part::Feature] Part__Feature190  label="pp3_battery013"
  shape: bbox 0.8457 x 25.33 x 15.74 mm, 1 faces, 0 solids (baked)
FEATURE [Part::Feature] Part__Feature191  label="pp3_battery014"
  shape: bbox 0.0001967 x 6.334 x 2.965e-07 mm, 1 faces, 0 solids (baked)
FEATURE [Part::Feature] Part__Feature192  label="pp3_battery015"
  shape: bbox 0.0001965 x 6.345 x 2.963e-07 mm, 1 faces, 0 solids (baked)
FEATURE [Part::Feature] Part__Feature193  label="pp3_battery016"
  shape: bbox 0.0001967 x 6.334 x 2.965e-07 mm, 1 faces, 0 solids (baked)
FEATURE [Part::Feature] Part__Feature194  label="pp3_battery017"
  shape: bbox 3 x 8.776 x 7.6 mm, 28 faces, 0 solids (baked)
FEATURE [App::Part] pp3_battery001  label="pp3_battery018"
  Group = -> [Part__Feature186,Part__Feature187,Part__Feature188,Part__Feature189,Part__Feature190,Part__Feature191,Part__Feature192,Part__Feature193,Part__Feature194]
  Origin = -> Origin011
  Placement = pos=(-1.1e-15,-5,-23) rot=(0,0,1;1.5708rad)
FEATURE [Sketcher::SketchObject] Sketch
  FullyConstrained = false
  Placement = pos=(0,0,0) rot=(0.57735,0.57735,0.57735;2.0944rad)
  sketch-geometry (4):
    g0: LineSegment StartX=-30 StartY=24.3147 StartZ=0 EndX=30 EndY=24.3147 EndZ=0
    g1: LineSegment StartX=30 StartY=24.3147 StartZ=0 EndX=30 EndY=-19.6853 EndZ=0
    g2: LineSegment StartX=30 StartY=-19.6853 StartZ=0 EndX=-30 EndY=-19.6853 EndZ=0
    g3: LineSegment StartX=-30 StartY=-19.6853 StartZ=0 EndX=-30 EndY=24.3147 EndZ=0
  constraints (10):
    c: Coincident(g0,g1)
    c: Coincident(g1,g2)
    c: Coincident(g2,g3)
    c: Coincident(g3,g0)
    c: Horizontal(g2)
    c: Vertical(g1)
    c: Vertical(g3)
    c: DistanceX(g0,g0) = 60
    c: DistanceY(g1,g1) = 44
    c: Symmetric(g0,g0,g-2)
FEATURE [Sketcher::SketchObject] Sketch001
  FullyConstrained = true
  sketch-geometry (4):
    g0: LineSegment StartX=-30 StartY=30 StartZ=0 EndX=30 EndY=30 EndZ=0
    g1: LineSegment StartX=30 StartY=30 StartZ=0 EndX=30 EndY=-30 EndZ=0
    g2: LineSegment StartX=30 StartY=-30 StartZ=0 EndX=-30 EndY=-30 EndZ=0
    g3: LineSegment StartX=-30 StartY=-30 StartZ=0 EndX=-30 EndY=30 EndZ=0
  constraints (10):
    c: Coincident(g0,g1)
    c: Coincident(g1,g2)
    c: Coincident(g2,g3)
    c: Coincident(g3,g0)
    c: Horizontal(g2)
    c: Vertical(g1)
    c: Symmetric(g0,g0,g-2)
    c: Symmetric(g2,g0,g-1)
    c: DistanceX(g0,g0) = 60
    c: DistanceY(g3,g3) = 60
